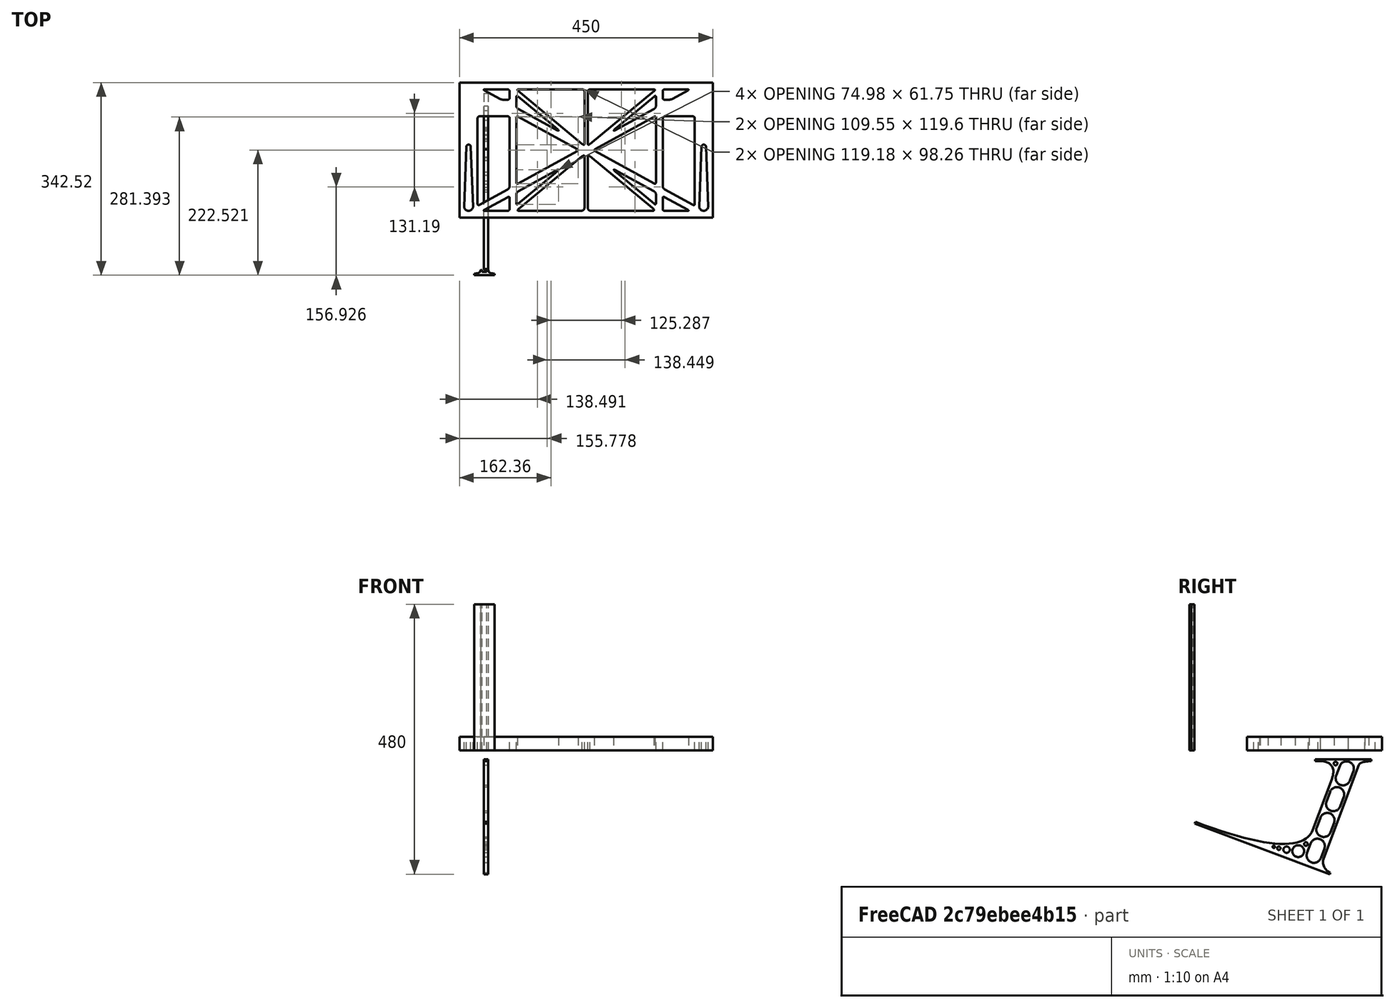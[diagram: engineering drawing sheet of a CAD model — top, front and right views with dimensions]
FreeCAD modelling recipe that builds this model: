
FCSTD DOCUMENT  (FreeCAD 0.19R0.19.2)
Label: laptopStand154FCStd
License: All rights reserved
LicenseURL: http://en.wikipedia.org/wiki/All_rights_reserved
objects: Sketcher::SketchObject×4, Part::Extrusion×3
note: 7 computed .brp shape members not serialized (recipe doc carries the construction recipe); baked Part::Feature solids carry a one-line shape summary decoded from their .brp

FEATURE [Sketcher::SketchObject] Sketch
  FullyConstrained = false
  sketch-geometry (349):
    g0: LineSegment StartX=-10.9272 StartY=-82.7794 StartZ=0 EndX=46.0728 EndY=-51.4823 EndZ=0
    g1: LineSegment StartX=-10.9272 StartY=76.4095 StartZ=0 EndX=-10.9272 EndY=-82.7794 EndZ=0
    g2: LineSegment StartX=46.0728 StartY=76.4095 StartZ=0 EndX=46.0728 EndY=-51.4823 EndZ=0
    g3: LineSegment StartX=-42.9272 StartY=136.221 StartZ=0 EndX=-42.9272 EndY=-103.779 EndZ=0
    g4: LineSegment StartX=407.073 StartY=136.221 StartZ=0 EndX=407.073 EndY=-103.779 EndZ=0
    g5: ArcOfCircle CenterX=-26.9272 CenterY=-83.7794 CenterZ=0 NormalX=0 NormalY=0 NormalZ=1 AngleXU=0 Radius=8 StartAngle=3.14159 EndAngle=6.28319
    g6: ArcOfCircle CenterX=391.073 CenterY=22.1087 CenterZ=0 NormalX=0 NormalY=0 NormalZ=1 AngleXU=0 Radius=8 StartAngle=-4.4e-15 EndAngle=3.14159
    g7: LineSegment StartX=399.073 StartY=22.1087 StartZ=0 EndX=399.073 EndY=-83.7794 EndZ=0
    g8: LineSegment StartX=383.073 StartY=22.1087 StartZ=0 EndX=383.073 EndY=-83.7794 EndZ=0
    g9: ArcOfCircle CenterX=391.073 CenterY=-83.7794 CenterZ=0 NormalX=0 NormalY=0 NormalZ=1 AngleXU=0 Radius=8 StartAngle=3.14159 EndAngle=6.28319
    g10: Circle CenterX=175.022 CenterY=27.0628 CenterZ=0 NormalX=0 NormalY=0 NormalZ=1 AngleXU=0 Radius=1
    g11: Circle CenterX=179.022 CenterY=24.8665 CenterZ=0 NormalX=0 NormalY=0 NormalZ=1 AngleXU=0 Radius=1
    g12: Circle CenterX=179.022 CenterY=27.0628 CenterZ=0 NormalX=0 NormalY=0 NormalZ=1 AngleXU=0 Radius=1
    g13: BSplineCurve PolesCount=3 KnotsCount=2 Degree=2 IsPeriodic=0
    g14: GeomPoint X=175.022 Y=27.0628 Z=0
    g15: GeomPoint X=179.022 Y=27.0628 Z=0
    g16: Circle CenterX=189.124 CenterY=27.0628 CenterZ=0 NormalX=0 NormalY=0 NormalZ=1 AngleXU=0 Radius=1
    g17: Circle CenterX=185.124 CenterY=24.8665 CenterZ=0 NormalX=0 NormalY=0 NormalZ=1 AngleXU=0 Radius=1
    g18: Circle CenterX=185.124 CenterY=27.0628 CenterZ=0 NormalX=0 NormalY=0 NormalZ=1 AngleXU=0 Radius=1
    g19: BSplineCurve PolesCount=3 KnotsCount=2 Degree=2 IsPeriodic=0
    g20: GeomPoint X=189.124 Y=27.0628 Z=0
    g21: GeomPoint X=185.124 Y=27.0628 Z=0
    g22: Circle CenterX=175.022 CenterY=5.37834 CenterZ=0 NormalX=0 NormalY=0 NormalZ=1 AngleXU=0 Radius=1
    g23: Circle CenterX=179.022 CenterY=7.57463 CenterZ=0 NormalX=0 NormalY=0 NormalZ=1 AngleXU=0 Radius=1
    g24: Circle CenterX=179.022 CenterY=5.34704 CenterZ=0 NormalX=0 NormalY=0 NormalZ=1 AngleXU=0 Radius=1
    g25: BSplineCurve PolesCount=3 KnotsCount=2 Degree=2 IsPeriodic=0
    g26: GeomPoint X=175.022 Y=5.37834 Z=0
    g27: GeomPoint X=179.022 Y=5.34704 Z=0
    g28: Circle CenterX=189.124 CenterY=5.37834 CenterZ=0 NormalX=0 NormalY=0 NormalZ=1 AngleXU=0 Radius=1
    g29: Circle CenterX=185.124 CenterY=7.57463 CenterZ=0 NormalX=0 NormalY=0 NormalZ=1 AngleXU=0 Radius=1
    g30: Circle CenterX=185.124 CenterY=5.34704 CenterZ=0 NormalX=0 NormalY=0 NormalZ=1 AngleXU=0 Radius=1
    g31: BSplineCurve PolesCount=3 KnotsCount=2 Degree=2 IsPeriodic=0
    g32: GeomPoint X=189.124 Y=5.37834 Z=0
    g33: GeomPoint X=185.124 Y=5.34704 Z=0
    g34: Circle CenterX=165.871 CenterY=18.1458 CenterZ=0 NormalX=0 NormalY=0 NormalZ=1 AngleXU=0 Radius=1
    g35: Circle CenterX=169.377 CenterY=16.2206 CenterZ=0 NormalX=0 NormalY=0 NormalZ=1 AngleXU=0 Radius=1
    g36: Circle CenterX=165.871 CenterY=14.2954 CenterZ=0 NormalX=0 NormalY=0 NormalZ=1 AngleXU=0 Radius=1
    g37: BSplineCurve PolesCount=3 KnotsCount=2 Degree=2 IsPeriodic=0
    g38: GeomPoint X=165.871 Y=18.1458 Z=0
    g39: GeomPoint X=165.871 Y=14.2954 Z=0
    g40: Circle CenterX=198.275 CenterY=18.1458 CenterZ=0 NormalX=0 NormalY=0 NormalZ=1 AngleXU=0 Radius=1
    g41: Circle CenterX=194.768 CenterY=16.2206 CenterZ=0 NormalX=0 NormalY=0 NormalZ=1 AngleXU=0 Radius=1
    g42: Circle CenterX=198.275 CenterY=14.2954 CenterZ=0 NormalX=0 NormalY=0 NormalZ=1 AngleXU=0 Radius=1
    g43: BSplineCurve PolesCount=3 KnotsCount=2 Degree=2 IsPeriodic=0
    g44: GeomPoint X=198.275 Y=18.1458 Z=0
    g45: GeomPoint X=198.275 Y=14.2954 Z=0
    g46: LineSegment StartX=407.073 StartY=-103.779 StartZ=0 EndX=-42.9272 EndY=-103.779 EndZ=0
    g47: LineSegment StartX=407.073 StartY=136.221 StartZ=0 EndX=-42.9272 EndY=136.221 EndZ=0
    g48: LineSegment StartX=46.0728 StartY=76.4095 StartZ=0 EndX=-10.9272 EndY=76.4095 EndZ=0
    g49: Circle CenterX=125.607 CenterY=54.1951 CenterZ=0 NormalX=0 NormalY=0 NormalZ=1 AngleXU=0 Radius=1
    g50: Circle CenterX=139.632 CenterY=46.4944 CenterZ=0 NormalX=0 NormalY=0 NormalZ=1 AngleXU=0 Radius=1
    g51: Circle CenterX=127.326 CenterY=56.7187 CenterZ=0 NormalX=0 NormalY=0 NormalZ=1 AngleXU=0 Radius=1
    g52: BSplineCurve PolesCount=3 KnotsCount=2 Degree=2 IsPeriodic=0
    g53: GeomPoint X=125.607 Y=54.1951 Z=0
    g54: GeomPoint X=127.326 Y=56.7187 Z=0
    g55: Circle CenterX=236.821 CenterY=56.7187 CenterZ=0 NormalX=0 NormalY=0 NormalZ=1 AngleXU=0 Radius=1
    g56: Circle CenterX=224.513 CenterY=46.4944 CenterZ=0 NormalX=0 NormalY=0 NormalZ=1 AngleXU=0 Radius=1
    g57: Circle CenterX=238.538 CenterY=54.1951 CenterZ=0 NormalX=0 NormalY=0 NormalZ=1 AngleXU=0 Radius=1
    g58: BSplineCurve PolesCount=3 KnotsCount=2 Degree=2 IsPeriodic=0
    g59: GeomPoint X=236.821 Y=56.7187 Z=0
    g60: GeomPoint X=238.538 Y=54.1951 Z=0
    g61: Circle CenterX=238.538 CenterY=-21.7539 CenterZ=0 NormalX=0 NormalY=0 NormalZ=1 AngleXU=0 Radius=1
    g62: Circle CenterX=224.513 CenterY=-14.0532 CenterZ=0 NormalX=0 NormalY=0 NormalZ=1 AngleXU=0 Radius=1
    g63: Circle CenterX=236.821 CenterY=-24.2775 CenterZ=0 NormalX=0 NormalY=0 NormalZ=1 AngleXU=0 Radius=1
    g64: BSplineCurve PolesCount=3 KnotsCount=2 Degree=2 IsPeriodic=0
    g65: GeomPoint X=238.538 Y=-21.7539 Z=0
    g66: GeomPoint X=236.821 Y=-24.2775 Z=0
    g67: Circle CenterX=125.607 CenterY=-21.7539 CenterZ=0 NormalX=0 NormalY=0 NormalZ=1 AngleXU=0 Radius=1
    g68: Circle CenterX=139.632 CenterY=-14.0532 CenterZ=0 NormalX=0 NormalY=0 NormalZ=1 AngleXU=0 Radius=1
    g69: Circle CenterX=127.325 CenterY=-24.2775 CenterZ=0 NormalX=0 NormalY=0 NormalZ=1 AngleXU=0 Radius=1
    g70: BSplineCurve PolesCount=3 KnotsCount=2 Degree=2 IsPeriodic=0
    g71: GeomPoint X=125.607 Y=-21.7539 Z=0
    g72: GeomPoint X=127.325 Y=-24.2775 Z=0
    g73: Circle CenterX=302.996 CenterY=111.695 CenterZ=0 NormalX=0 NormalY=0 NormalZ=1 AngleXU=0 Radius=1
    g74: Circle CenterX=306.073 CenterY=114.251 CenterZ=0 NormalX=0 NormalY=0 NormalZ=1 AngleXU=0 Radius=1
    g75: Circle CenterX=306.073 CenterY=110.251 CenterZ=0 NormalX=0 NormalY=0 NormalZ=1 AngleXU=0 Radius=1
    g76: BSplineCurve PolesCount=3 KnotsCount=2 Degree=2 IsPeriodic=0
    g77: GeomPoint X=302.996 Y=111.695 Z=0
    g78: GeomPoint X=306.073 Y=110.251 Z=0
    g79: Circle CenterX=306.073 CenterY=95.2763 CenterZ=0 NormalX=0 NormalY=0 NormalZ=1 AngleXU=0 Radius=1
    g80: Circle CenterX=306.073 CenterY=91.2763 CenterZ=0 NormalX=0 NormalY=0 NormalZ=1 AngleXU=0 Radius=1
    g81: Circle CenterX=302.567 CenterY=89.3511 CenterZ=0 NormalX=0 NormalY=0 NormalZ=1 AngleXU=0 Radius=1
    g82: BSplineCurve PolesCount=3 KnotsCount=2 Degree=2 IsPeriodic=0
    g83: GeomPoint X=306.073 Y=95.2763 Z=0
    g84: GeomPoint X=302.567 Y=89.3511 Z=0
    g85: LineSegment StartX=306.073 StartY=110.251 StartZ=0 EndX=306.073 EndY=95.2763 EndZ=0
    g86: LineSegment StartX=302.996 StartY=111.695 StartZ=0 EndX=236.821 EndY=56.7187 EndZ=0
    g87: LineSegment StartX=238.538 StartY=54.1951 StartZ=0 EndX=302.567 EndY=89.3511 EndZ=0
    g88: Circle CenterX=61.1496 CenterY=111.695 CenterZ=0 NormalX=0 NormalY=0 NormalZ=1 AngleXU=0 Radius=1
    g89: Circle CenterX=58.0728 CenterY=114.251 CenterZ=0 NormalX=0 NormalY=0 NormalZ=1 AngleXU=0 Radius=1
    g90: Circle CenterX=58.0728 CenterY=110.251 CenterZ=0 NormalX=0 NormalY=0 NormalZ=1 AngleXU=0 Radius=1
    g91: BSplineCurve PolesCount=3 KnotsCount=2 Degree=2 IsPeriodic=0
    g92: GeomPoint X=61.1496 Y=111.695 Z=0
    g93: GeomPoint X=58.0728 Y=110.251 Z=0
    g94: Circle CenterX=61.5791 CenterY=89.3511 CenterZ=0 NormalX=0 NormalY=0 NormalZ=1 AngleXU=0 Radius=1
    g95: Circle CenterX=58.0728 CenterY=91.2763 CenterZ=0 NormalX=0 NormalY=0 NormalZ=1 AngleXU=0 Radius=1
    g96: Circle CenterX=58.0728 CenterY=95.2763 CenterZ=0 NormalX=0 NormalY=0 NormalZ=1 AngleXU=0 Radius=1
    g97: BSplineCurve PolesCount=3 KnotsCount=2 Degree=2 IsPeriodic=0
    g98: GeomPoint X=61.5791 Y=89.3511 Z=0
    g99: GeomPoint X=58.0728 Y=95.2763 Z=0
    g100: LineSegment StartX=58.0728 StartY=110.251 StartZ=0 EndX=58.0728 EndY=95.2763 EndZ=0
    g101: LineSegment StartX=61.1496 StartY=111.695 StartZ=0 EndX=127.326 EndY=56.7187 EndZ=0
    g102: LineSegment StartX=125.607 StartY=54.1951 StartZ=0 EndX=61.5791 EndY=89.3511 EndZ=0
    g103: Circle CenterX=61.5791 CenterY=-56.9099 CenterZ=0 NormalX=0 NormalY=0 NormalZ=1 AngleXU=0 Radius=1
    g104: Circle CenterX=58.0728 CenterY=-58.8351 CenterZ=0 NormalX=0 NormalY=0 NormalZ=1 AngleXU=0 Radius=1
    g105: Circle CenterX=58.0728 CenterY=-62.8351 CenterZ=0 NormalX=0 NormalY=0 NormalZ=1 AngleXU=0 Radius=1
    g106: BSplineCurve PolesCount=3 KnotsCount=2 Degree=2 IsPeriodic=0
    g107: GeomPoint X=61.5791 Y=-56.9099 Z=0
    g108: GeomPoint X=58.0728 Y=-62.8351 Z=0
    g109: Circle CenterX=58.0728 CenterY=-77.8102 CenterZ=0 NormalX=0 NormalY=0 NormalZ=1 AngleXU=0 Radius=1
    g110: Circle CenterX=58.0728 CenterY=-81.8102 CenterZ=0 NormalX=0 NormalY=0 NormalZ=1 AngleXU=0 Radius=1
    g111: Circle CenterX=61.1496 CenterY=-79.2541 CenterZ=0 NormalX=0 NormalY=0 NormalZ=1 AngleXU=0 Radius=1
    g112: BSplineCurve PolesCount=3 KnotsCount=2 Degree=2 IsPeriodic=0
    g113: GeomPoint X=58.0728 Y=-77.8102 Z=0
    g114: GeomPoint X=61.1496 Y=-79.2541 Z=0
    g115: LineSegment StartX=58.0728 StartY=-62.8351 StartZ=0 EndX=58.0728 EndY=-77.8102 EndZ=0
    g116: LineSegment StartX=61.1496 StartY=-79.2541 StartZ=0 EndX=127.325 EndY=-24.2775 EndZ=0
    g117: LineSegment StartX=125.607 StartY=-21.7539 StartZ=0 EndX=61.5791 EndY=-56.9099 EndZ=0
    g118: Circle CenterX=302.567 CenterY=-56.9099 CenterZ=0 NormalX=0 NormalY=0 NormalZ=1 AngleXU=0 Radius=1
    g119: Circle CenterX=306.073 CenterY=-58.8351 CenterZ=0 NormalX=0 NormalY=0 NormalZ=1 AngleXU=0 Radius=1
    g120: Circle CenterX=306.073 CenterY=-62.8351 CenterZ=0 NormalX=0 NormalY=0 NormalZ=1 AngleXU=0 Radius=1
    g121: BSplineCurve PolesCount=3 KnotsCount=2 Degree=2 IsPeriodic=0
    g122: GeomPoint X=302.567 Y=-56.9099 Z=0
    g123: GeomPoint X=306.073 Y=-62.8351 Z=0
    g124: Circle CenterX=302.996 CenterY=-79.2541 CenterZ=0 NormalX=0 NormalY=0 NormalZ=1 AngleXU=0 Radius=1
    g125: Circle CenterX=306.073 CenterY=-81.8102 CenterZ=0 NormalX=0 NormalY=0 NormalZ=1 AngleXU=0 Radius=1
    g126: Circle CenterX=306.073 CenterY=-77.8102 CenterZ=0 NormalX=0 NormalY=0 NormalZ=1 AngleXU=0 Radius=1
    g127: BSplineCurve PolesCount=3 KnotsCount=2 Degree=2 IsPeriodic=0
    g128: GeomPoint X=302.996 Y=-79.2541 Z=0
    g129: GeomPoint X=306.073 Y=-77.8102 Z=0
    g130: LineSegment StartX=306.073 StartY=-62.8351 StartZ=0 EndX=306.073 EndY=-77.8102 EndZ=0
    g131: LineSegment StartX=302.996 StartY=-79.2541 StartZ=0 EndX=236.821 EndY=-24.2775 EndZ=0
    g132: LineSegment StartX=238.538 StartY=-21.7539 StartZ=0 EndX=302.567 EndY=-56.9099 EndZ=0
    g133: Circle CenterX=61.6457 CenterY=-88.8112 CenterZ=0 NormalX=0 NormalY=0 NormalZ=1 AngleXU=0 Radius=1
    g134: Circle CenterX=58.0728 CenterY=-91.7794 CenterZ=0 NormalX=0 NormalY=0 NormalZ=1 AngleXU=0 Radius=1
    g135: Circle CenterX=63.9135 CenterY=-91.7794 CenterZ=0 NormalX=0 NormalY=0 NormalZ=1 AngleXU=0 Radius=1
    g136: BSplineCurve PolesCount=3 KnotsCount=2 Degree=2 IsPeriodic=0
    g137: GeomPoint X=61.6457 Y=-88.8112 Z=0
    g138: GeomPoint X=63.9135 Y=-91.7794 Z=0
    g139: Circle CenterX=179.022 CenterY=-85.8163 CenterZ=0 NormalX=0 NormalY=0 NormalZ=1 AngleXU=0 Radius=1
    g140: Circle CenterX=179.022 CenterY=-91.7794 CenterZ=0 NormalX=0 NormalY=0 NormalZ=1 AngleXU=0 Radius=1
    g141: Circle CenterX=171.895 CenterY=-91.7794 CenterZ=0 NormalX=0 NormalY=0 NormalZ=1 AngleXU=0 Radius=1
    g142: BSplineCurve PolesCount=3 KnotsCount=2 Degree=2 IsPeriodic=0
    g143: GeomPoint X=179.022 Y=-85.8163 Z=0
    g144: GeomPoint X=171.895 Y=-91.7794 Z=0
    g145: Circle CenterX=185.124 CenterY=-86.2028 CenterZ=0 NormalX=0 NormalY=0 NormalZ=1 AngleXU=0 Radius=1
    g146: Circle CenterX=185.124 CenterY=-91.7794 CenterZ=0 NormalX=0 NormalY=0 NormalZ=1 AngleXU=0 Radius=1
    g147: Circle CenterX=191.747 CenterY=-91.7794 CenterZ=0 NormalX=0 NormalY=0 NormalZ=1 AngleXU=0 Radius=1
    g148: BSplineCurve PolesCount=3 KnotsCount=2 Degree=2 IsPeriodic=0
    g149: GeomPoint X=185.124 Y=-86.2028 Z=0
    g150: GeomPoint X=191.747 Y=-91.7794 Z=0
    g151: Circle CenterX=299.888 CenterY=-86.6413 CenterZ=0 NormalX=0 NormalY=0 NormalZ=1 AngleXU=0 Radius=1
    g152: Circle CenterX=306.073 CenterY=-91.7794 CenterZ=0 NormalX=0 NormalY=0 NormalZ=1 AngleXU=0 Radius=1
    g153: Circle CenterX=298.776 CenterY=-91.7794 CenterZ=0 NormalX=0 NormalY=0 NormalZ=1 AngleXU=0 Radius=1
    g154: BSplineCurve PolesCount=3 KnotsCount=2 Degree=2 IsPeriodic=0
    g155: GeomPoint X=299.888 Y=-86.6413 Z=0
    g156: GeomPoint X=298.776 Y=-91.7794 Z=0
    g157: LineSegment StartX=189.124 StartY=5.37834 StartZ=0 EndX=299.888 EndY=-86.6413 EndZ=0
    g158: LineSegment StartX=298.776 StartY=-91.7794 StartZ=0 EndX=191.747 EndY=-91.7794 EndZ=0
    g159: LineSegment StartX=185.124 StartY=-86.2028 StartZ=0 EndX=185.124 EndY=5.34704 EndZ=0
    g160: LineSegment StartX=179.022 StartY=5.34704 StartZ=0 EndX=179.022 EndY=-85.8163 EndZ=0
    g161: LineSegment StartX=171.895 StartY=-91.7794 StartZ=0 EndX=63.9135 EndY=-91.7794 EndZ=0
    g162: LineSegment StartX=61.6457 StartY=-88.8112 StartZ=0 EndX=175.022 EndY=5.37834 EndZ=0
    g163: Circle CenterX=302.073 CenterY=124.221 CenterZ=0 NormalX=0 NormalY=0 NormalZ=1 AngleXU=0 Radius=1
    g164: Circle CenterX=306.073 CenterY=124.221 CenterZ=0 NormalX=0 NormalY=0 NormalZ=1 AngleXU=0 Radius=1
    g165: Circle CenterX=302.996 CenterY=121.665 CenterZ=0 NormalX=0 NormalY=0 NormalZ=1 AngleXU=0 Radius=1
    g166: BSplineCurve PolesCount=3 KnotsCount=2 Degree=2 IsPeriodic=0
    g167: GeomPoint X=302.073 Y=124.221 Z=0
    g168: GeomPoint X=302.996 Y=121.665 Z=0
    g169: Circle CenterX=189.124 CenterY=124.221 CenterZ=0 NormalX=0 NormalY=0 NormalZ=1 AngleXU=0 Radius=1
    g170: Circle CenterX=185.124 CenterY=124.221 CenterZ=0 NormalX=0 NormalY=0 NormalZ=1 AngleXU=0 Radius=1
    g171: Circle CenterX=185.124 CenterY=120.221 CenterZ=0 NormalX=0 NormalY=0 NormalZ=1 AngleXU=0 Radius=1
    g172: BSplineCurve PolesCount=3 KnotsCount=2 Degree=2 IsPeriodic=0
    g173: GeomPoint X=189.124 Y=124.221 Z=0
    g174: GeomPoint X=185.124 Y=120.221 Z=0
    g175: Circle CenterX=175.022 CenterY=124.221 CenterZ=0 NormalX=0 NormalY=0 NormalZ=1 AngleXU=0 Radius=1
    g176: Circle CenterX=179.022 CenterY=124.221 CenterZ=0 NormalX=0 NormalY=0 NormalZ=1 AngleXU=0 Radius=1
    g177: Circle CenterX=179.022 CenterY=120.221 CenterZ=0 NormalX=0 NormalY=0 NormalZ=1 AngleXU=0 Radius=1
    g178: BSplineCurve PolesCount=3 KnotsCount=2 Degree=2 IsPeriodic=0
    g179: GeomPoint X=175.022 Y=124.221 Z=0
    g180: GeomPoint X=179.022 Y=120.221 Z=0
    g181: Circle CenterX=62.0728 CenterY=124.221 CenterZ=0 NormalX=0 NormalY=0 NormalZ=1 AngleXU=0 Radius=1
    g182: Circle CenterX=58.0728 CenterY=124.221 CenterZ=0 NormalX=0 NormalY=0 NormalZ=1 AngleXU=0 Radius=1
    g183: Circle CenterX=61.1496 CenterY=121.665 CenterZ=0 NormalX=0 NormalY=0 NormalZ=1 AngleXU=0 Radius=1
    g184: BSplineCurve PolesCount=3 KnotsCount=2 Degree=2 IsPeriodic=0
    g185: GeomPoint X=62.0728 Y=124.221 Z=0
    g186: GeomPoint X=61.1496 Y=121.665 Z=0
    g187: LineSegment StartX=62.0728 StartY=124.221 StartZ=0 EndX=175.022 EndY=124.221 EndZ=0
    g188: LineSegment StartX=179.022 StartY=120.221 StartZ=0 EndX=179.022 EndY=27.0628 EndZ=0
    g189: LineSegment StartX=185.124 StartY=27.0628 StartZ=0 EndX=185.124 EndY=120.221 EndZ=0
    g190: LineSegment StartX=189.124 StartY=124.221 StartZ=0 EndX=302.073 EndY=124.221 EndZ=0
    g191: LineSegment StartX=302.996 StartY=121.665 StartZ=0 EndX=189.124 EndY=27.0628 EndZ=0
    g192: LineSegment StartX=175.022 StartY=27.0628 StartZ=0 EndX=61.1496 EndY=121.665 EndZ=0
    g193: Circle CenterX=61.5791 CenterY=75.4095 CenterZ=0 NormalX=0 NormalY=0 NormalZ=1 AngleXU=0 Radius=1
    g194: Circle CenterX=58.0728 CenterY=77.3346 CenterZ=0 NormalX=0 NormalY=0 NormalZ=1 AngleXU=0 Radius=1
    g195: Circle CenterX=58.0728 CenterY=73.3346 CenterZ=0 NormalX=0 NormalY=0 NormalZ=1 AngleXU=0 Radius=1
    g196: BSplineCurve PolesCount=3 KnotsCount=2 Degree=2 IsPeriodic=0
    g197: GeomPoint X=61.5791 Y=75.4095 Z=0
    g198: GeomPoint X=58.0728 Y=73.3346 Z=0
    g199: Circle CenterX=58.0728 CenterY=-40.8935 CenterZ=0 NormalX=0 NormalY=0 NormalZ=1 AngleXU=0 Radius=1
    g200: Circle CenterX=58.0728 CenterY=-44.8935 CenterZ=0 NormalX=0 NormalY=0 NormalZ=1 AngleXU=0 Radius=1
    g201: Circle CenterX=61.5791 CenterY=-42.9683 CenterZ=0 NormalX=0 NormalY=0 NormalZ=1 AngleXU=0 Radius=1
    g202: BSplineCurve PolesCount=3 KnotsCount=2 Degree=2 IsPeriodic=0
    g203: GeomPoint X=58.0728 Y=-40.8935 Z=0
    g204: GeomPoint X=61.5791 Y=-42.9683 Z=0
    g205: LineSegment StartX=61.5791 StartY=-42.9683 StartZ=0 EndX=165.871 EndY=14.2954 EndZ=0
    g206: LineSegment StartX=165.871 StartY=18.1458 StartZ=0 EndX=61.5791 EndY=75.4095 EndZ=0
    g207: LineSegment StartX=58.0728 StartY=73.3346 StartZ=0 EndX=58.0728 EndY=-40.8935 EndZ=0
    g208: Circle CenterX=302.567 CenterY=-42.9683 CenterZ=0 NormalX=0 NormalY=0 NormalZ=1 AngleXU=0 Radius=1
    g209: Circle CenterX=306.073 CenterY=-44.8935 CenterZ=0 NormalX=0 NormalY=0 NormalZ=1 AngleXU=0 Radius=1
    g210: Circle CenterX=306.073 CenterY=-40.8935 CenterZ=0 NormalX=0 NormalY=0 NormalZ=1 AngleXU=0 Radius=1
    g211: BSplineCurve PolesCount=3 KnotsCount=2 Degree=2 IsPeriodic=0
    g212: GeomPoint X=302.567 Y=-42.9683 Z=0
    g213: GeomPoint X=306.073 Y=-40.8935 Z=0
    g214: Circle CenterX=306.073 CenterY=73.3346 CenterZ=0 NormalX=0 NormalY=0 NormalZ=1 AngleXU=0 Radius=1
    g215: Circle CenterX=306.073 CenterY=77.3346 CenterZ=0 NormalX=0 NormalY=0 NormalZ=1 AngleXU=0 Radius=1
    g216: Circle CenterX=302.567 CenterY=75.4095 CenterZ=0 NormalX=0 NormalY=0 NormalZ=1 AngleXU=0 Radius=1
    g217: BSplineCurve PolesCount=3 KnotsCount=2 Degree=2 IsPeriodic=0
    g218: GeomPoint X=306.073 Y=73.3346 Z=0
    g219: GeomPoint X=302.567 Y=75.4095 Z=0
    g220: LineSegment StartX=302.567 StartY=-42.9683 StartZ=0 EndX=198.275 EndY=14.2954 EndZ=0
    g221: LineSegment StartX=198.275 StartY=18.1458 StartZ=0 EndX=302.567 EndY=75.4095 EndZ=0
    g222: LineSegment StartX=306.073 StartY=73.3346 StartZ=0 EndX=306.073 EndY=-40.8935 EndZ=0
    g223: LineSegment StartX=322.073 StartY=105.865 StartZ=0 EndX=328.643 EndY=105.865 EndZ=0
    g224: LineSegment StartX=318.073 StartY=120.221 StartZ=0 EndX=318.073 EndY=109.865 EndZ=0
    g225: LineSegment StartX=336.157 StartY=107.779 StartZ=0 EndX=362.567 EndY=122.294 EndZ=0
    g226: Circle CenterX=362.073 CenterY=124.221 CenterZ=0 NormalX=0 NormalY=0 NormalZ=1 AngleXU=0 Radius=1
    g227: Circle CenterX=366.073 CenterY=124.221 CenterZ=0 NormalX=0 NormalY=0 NormalZ=1 AngleXU=0 Radius=1
    g228: Circle CenterX=362.567 CenterY=122.294 CenterZ=0 NormalX=0 NormalY=0 NormalZ=1 AngleXU=0 Radius=1
    g229: BSplineCurve PolesCount=3 KnotsCount=2 Degree=2 IsPeriodic=0
    g230: GeomPoint X=362.073 Y=124.221 Z=0
    g231: GeomPoint X=362.567 Y=122.294 Z=0
    g232: Circle CenterX=322.073 CenterY=124.221 CenterZ=0 NormalX=0 NormalY=0 NormalZ=1 AngleXU=0 Radius=1
    g233: Circle CenterX=318.073 CenterY=124.221 CenterZ=0 NormalX=0 NormalY=0 NormalZ=1 AngleXU=0 Radius=1
    g234: Circle CenterX=318.073 CenterY=120.221 CenterZ=0 NormalX=0 NormalY=0 NormalZ=1 AngleXU=0 Radius=1
    g235: BSplineCurve PolesCount=3 KnotsCount=2 Degree=2 IsPeriodic=0
    g236: GeomPoint X=322.073 Y=124.221 Z=0
    g237: GeomPoint X=318.073 Y=120.221 Z=0
    g238: Circle CenterX=322.073 CenterY=105.865 CenterZ=0 NormalX=0 NormalY=0 NormalZ=1 AngleXU=0 Radius=1
    g239: Circle CenterX=318.073 CenterY=105.865 CenterZ=0 NormalX=0 NormalY=0 NormalZ=1 AngleXU=0 Radius=1
    g240: Circle CenterX=318.073 CenterY=109.865 CenterZ=0 NormalX=0 NormalY=0 NormalZ=1 AngleXU=0 Radius=1
    g241: BSplineCurve PolesCount=3 KnotsCount=2 Degree=2 IsPeriodic=0
    g242: GeomPoint X=322.073 Y=105.865 Z=0
    g243: GeomPoint X=318.073 Y=109.865 Z=0
    g244: Circle CenterX=336.157 CenterY=107.779 CenterZ=0 NormalX=0 NormalY=0 NormalZ=1 AngleXU=0 Radius=1
    g245: Circle CenterX=332.651 CenterY=105.853 CenterZ=0 NormalX=0 NormalY=0 NormalZ=1 AngleXU=0 Radius=1
    g246: Circle CenterX=328.643 CenterY=105.865 CenterZ=0 NormalX=0 NormalY=0 NormalZ=1 AngleXU=0 Radius=1
    g247: BSplineCurve PolesCount=3 KnotsCount=2 Degree=2 IsPeriodic=0
    g248: GeomPoint X=336.157 Y=107.779 Z=0
    g249: GeomPoint X=328.643 Y=105.865 Z=0
    g250: LineSegment StartX=322.073 StartY=124.221 StartZ=0 EndX=362.073 EndY=124.221 EndZ=0
    g251: Circle CenterX=371.567 CenterY=-80.8644 CenterZ=0 NormalX=0 NormalY=0 NormalZ=1 AngleXU=0 Radius=1
    g252: Circle CenterX=375.073 CenterY=-82.7896 CenterZ=0 NormalX=0 NormalY=0 NormalZ=1 AngleXU=0 Radius=1
    g253: Circle CenterX=375.073 CenterY=-78.7896 CenterZ=0 NormalX=0 NormalY=0 NormalZ=1 AngleXU=0 Radius=1
    g254: BSplineCurve PolesCount=3 KnotsCount=2 Degree=2 IsPeriodic=0
    g255: GeomPoint X=371.567 Y=-80.8644 Z=0
    g256: GeomPoint X=375.073 Y=-78.7896 Z=0
    g257: Circle CenterX=321.579 CenterY=-53.4075 CenterZ=0 NormalX=0 NormalY=0 NormalZ=1 AngleXU=0 Radius=1
    g258: Circle CenterX=318.073 CenterY=-51.4823 CenterZ=0 NormalX=0 NormalY=0 NormalZ=1 AngleXU=0 Radius=1
    g259: Circle CenterX=318.073 CenterY=-47.4805 CenterZ=0 NormalX=0 NormalY=0 NormalZ=1 AngleXU=0 Radius=1
    g260: BSplineCurve PolesCount=3 KnotsCount=2 Degree=2 IsPeriodic=0
    g261: GeomPoint X=321.579 Y=-53.4075 Z=0
    g262: GeomPoint X=318.073 Y=-47.4805 Z=0
    g263: LineSegment StartX=371.567 StartY=-80.8644 StartZ=0 EndX=321.579 EndY=-53.4075 EndZ=0
    g264: Circle CenterX=321.579 CenterY=-67.3492 CenterZ=0 NormalX=0 NormalY=0 NormalZ=1 AngleXU=0 Radius=1
    g265: Circle CenterX=318.073 CenterY=-65.424 CenterZ=0 NormalX=0 NormalY=0 NormalZ=1 AngleXU=0 Radius=1
    g266: Circle CenterX=318.073 CenterY=-69.424 CenterZ=0 NormalX=0 NormalY=0 NormalZ=1 AngleXU=0 Radius=1
    g267: BSplineCurve PolesCount=3 KnotsCount=2 Degree=2 IsPeriodic=0
    g268: GeomPoint X=321.579 Y=-67.3492 Z=0
    g269: GeomPoint X=318.073 Y=-69.424 Z=0
    g270: Circle CenterX=362.567 CenterY=-89.8542 CenterZ=0 NormalX=0 NormalY=0 NormalZ=1 AngleXU=0 Radius=1
    g271: Circle CenterX=366.073 CenterY=-91.7794 CenterZ=0 NormalX=0 NormalY=0 NormalZ=1 AngleXU=0 Radius=1
    g272: Circle CenterX=362.073 CenterY=-91.7794 CenterZ=0 NormalX=0 NormalY=0 NormalZ=1 AngleXU=0 Radius=1
    g273: BSplineCurve PolesCount=3 KnotsCount=2 Degree=2 IsPeriodic=0
    g274: GeomPoint X=362.567 Y=-89.8542 Z=0
    g275: GeomPoint X=362.073 Y=-91.7794 Z=0
    g276: Circle CenterX=322.073 CenterY=-91.7794 CenterZ=0 NormalX=0 NormalY=0 NormalZ=1 AngleXU=0 Radius=1
    g277: Circle CenterX=318.073 CenterY=-91.7794 CenterZ=0 NormalX=0 NormalY=0 NormalZ=1 AngleXU=0 Radius=1
    g278: Circle CenterX=318.073 CenterY=-87.7794 CenterZ=0 NormalX=0 NormalY=0 NormalZ=1 AngleXU=0 Radius=1
    g279: BSplineCurve PolesCount=3 KnotsCount=2 Degree=2 IsPeriodic=0
    g280: GeomPoint X=322.073 Y=-91.7794 Z=0
    g281: GeomPoint X=318.073 Y=-87.7794 Z=0
    g282: LineSegment StartX=362.567 StartY=-89.8542 StartZ=0 EndX=321.579 EndY=-67.3492 EndZ=0
    g283: LineSegment StartX=318.073 StartY=-69.424 StartZ=0 EndX=318.073 EndY=-87.7794 EndZ=0
    g284: LineSegment StartX=322.073 StartY=-91.7794 StartZ=0 EndX=362.073 EndY=-91.7794 EndZ=0
    g285: Circle CenterX=2.07281 CenterY=124.221 CenterZ=0 NormalX=0 NormalY=0 NormalZ=1 AngleXU=0 Radius=1
    g286: Circle CenterX=1.57905 CenterY=122.295 CenterZ=0 NormalX=0 NormalY=0 NormalZ=1 AngleXU=0 Radius=1
    g287: BSplineCurve PolesCount=3 KnotsCount=2 Degree=2 IsPeriodic=0
    g288: GeomPoint X=2.07281 Y=124.221 Z=0
    g289: GeomPoint X=1.57905 Y=122.295 Z=0
    g290: Circle CenterX=42.0728 CenterY=124.221 CenterZ=0 NormalX=0 NormalY=0 NormalZ=1 AngleXU=0 Radius=1
    g291: Circle CenterX=46.0728 CenterY=124.221 CenterZ=0 NormalX=0 NormalY=0 NormalZ=1 AngleXU=0 Radius=1
    g292: Circle CenterX=46.0728 CenterY=120.221 CenterZ=0 NormalX=0 NormalY=0 NormalZ=1 AngleXU=0 Radius=1
    g293: BSplineCurve PolesCount=3 KnotsCount=2 Degree=2 IsPeriodic=0
    g294: GeomPoint X=42.0728 Y=124.221 Z=0
    g295: GeomPoint X=46.0728 Y=120.221 Z=0
    g296: Circle CenterX=46.0728 CenterY=109.865 CenterZ=0 NormalX=0 NormalY=0 NormalZ=1 AngleXU=0 Radius=1
    g297: Circle CenterX=46.0728 CenterY=105.865 CenterZ=0 NormalX=0 NormalY=0 NormalZ=1 AngleXU=0 Radius=1
    g298: Circle CenterX=42.0728 CenterY=105.865 CenterZ=0 NormalX=0 NormalY=0 NormalZ=1 AngleXU=0 Radius=1
    g299: BSplineCurve PolesCount=3 KnotsCount=2 Degree=2 IsPeriodic=0
    g300: GeomPoint X=46.0728 Y=109.865 Z=0
    g301: GeomPoint X=42.0728 Y=105.865 Z=0
    g302: Circle CenterX=35.5028 CenterY=105.865 CenterZ=0 NormalX=0 NormalY=0 NormalZ=1 AngleXU=0 Radius=1
    g303: Circle CenterX=31.5028 CenterY=105.865 CenterZ=0 NormalX=0 NormalY=0 NormalZ=1 AngleXU=0 Radius=1
    g304: Circle CenterX=27.9965 CenterY=107.79 CenterZ=0 NormalX=0 NormalY=0 NormalZ=1 AngleXU=0 Radius=1
    g305: BSplineCurve PolesCount=3 KnotsCount=2 Degree=2 IsPeriodic=0
    g306: GeomPoint X=35.5028 Y=105.865 Z=0
    g307: GeomPoint X=27.9965 Y=107.79 Z=0
    g308: LineSegment StartX=2.07281 StartY=124.221 StartZ=0 EndX=42.0728 EndY=124.221 EndZ=0
    g309: LineSegment StartX=46.0728 StartY=120.221 StartZ=0 EndX=46.0728 EndY=109.865 EndZ=0
    g310: LineSegment StartX=42.0728 StartY=105.865 StartZ=0 EndX=35.5028 EndY=105.865 EndZ=0
    g311: LineSegment StartX=27.9965 StartY=107.79 StartZ=0 EndX=1.57905 EndY=122.295 EndZ=0
    g312: Circle CenterX=42.5666 CenterY=-67.3492 CenterZ=0 NormalX=0 NormalY=0 NormalZ=1 AngleXU=0 Radius=1
    g313: Circle CenterX=46.0728 CenterY=-65.424 CenterZ=0 NormalX=0 NormalY=0 NormalZ=1 AngleXU=0 Radius=1
    g314: Circle CenterX=46.0728 CenterY=-69.424 CenterZ=0 NormalX=0 NormalY=0 NormalZ=1 AngleXU=0 Radius=1
    g315: BSplineCurve PolesCount=3 KnotsCount=2 Degree=2 IsPeriodic=0
    g316: GeomPoint X=42.5666 Y=-67.3492 Z=0
    g317: GeomPoint X=46.0728 Y=-69.424 Z=0
    g318: Circle CenterX=46.0728 CenterY=-87.7794 CenterZ=0 NormalX=0 NormalY=0 NormalZ=1 AngleXU=0 Radius=1
    g319: Circle CenterX=46.0728 CenterY=-91.7794 CenterZ=0 NormalX=0 NormalY=0 NormalZ=1 AngleXU=0 Radius=1
    g320: Circle CenterX=42.0728 CenterY=-91.7794 CenterZ=0 NormalX=0 NormalY=0 NormalZ=1 AngleXU=0 Radius=1
    g321: BSplineCurve PolesCount=3 KnotsCount=2 Degree=2 IsPeriodic=0
    g322: GeomPoint X=46.0728 Y=-87.7794 Z=0
    g323: GeomPoint X=42.0728 Y=-91.7794 Z=0
    g324: Circle CenterX=2.07281 CenterY=-91.7794 CenterZ=0 NormalX=0 NormalY=0 NormalZ=1 AngleXU=0 Radius=1
    g325: Circle CenterX=-1.92719 CenterY=-91.7794 CenterZ=0 NormalX=0 NormalY=0 NormalZ=1 AngleXU=0 Radius=1
    g326: Circle CenterX=1.57905 CenterY=-89.8542 CenterZ=0 NormalX=0 NormalY=0 NormalZ=1 AngleXU=0 Radius=1
    g327: BSplineCurve PolesCount=3 KnotsCount=2 Degree=2 IsPeriodic=0
    g328: GeomPoint X=2.07281 Y=-91.7794 Z=0
    g329: GeomPoint X=1.57905 Y=-89.8542 Z=0
    g330: LineSegment StartX=2.07281 StartY=-91.7794 StartZ=0 EndX=42.0728 EndY=-91.7794 EndZ=0
    g331: LineSegment StartX=46.0728 StartY=-87.7794 StartZ=0 EndX=46.0728 EndY=-69.424 EndZ=0
    g332: LineSegment StartX=42.5666 StartY=-67.3492 StartZ=0 EndX=1.57905 EndY=-89.8542 EndZ=0
    g333: Circle CenterX=322.073 CenterY=76.4095 CenterZ=0 NormalX=0 NormalY=0 NormalZ=1 AngleXU=0 Radius=4
    g334: BSplineCurve PolesCount=3 KnotsCount=2 Degree=2 IsPeriodic=0
    g335: GeomPoint X=318.073 Y=72.4095 Z=0
    g336: GeomPoint X=322.073 Y=76.4095 Z=0
    g337: Circle CenterX=375.073 CenterY=72.4095 CenterZ=0 NormalX=0 NormalY=0 NormalZ=1 AngleXU=0 Radius=1
    g338: Circle CenterX=375.073 CenterY=76.4095 CenterZ=0 NormalX=0 NormalY=0 NormalZ=1 AngleXU=0 Radius=1
    g339: Circle CenterX=371.073 CenterY=76.4095 CenterZ=0 NormalX=0 NormalY=0 NormalZ=1 AngleXU=0 Radius=1
    g340: BSplineCurve PolesCount=3 KnotsCount=2 Degree=2 IsPeriodic=0
    g341: GeomPoint X=375.073 Y=72.4095 Z=0
    g342: GeomPoint X=371.073 Y=76.4095 Z=0
    g343: LineSegment StartX=322.073 StartY=76.4095 StartZ=0 EndX=371.073 EndY=76.4095 EndZ=0
    g344: LineSegment StartX=318.073 StartY=72.4095 StartZ=0 EndX=318.073 EndY=-47.4805 EndZ=0
    g345: LineSegment StartX=375.073 StartY=72.4095 StartZ=0 EndX=375.073 EndY=-78.7896 EndZ=0
    g346: ArcOfCircle CenterX=-26.9272 CenterY=22.1087 CenterZ=0 NormalX=0 NormalY=0 NormalZ=1 AngleXU=0 Radius=4 StartAngle=5e-16 EndAngle=3.14159
    g347: LineSegment StartX=-30.9272 StartY=22.1087 StartZ=0 EndX=-34.9272 EndY=-83.7794 EndZ=0
    g348: LineSegment StartX=-18.9272 StartY=-83.7794 StartZ=0 EndX=-22.9272 EndY=22.1087 EndZ=0
  constraints (572):
    c: Coincident(g0,g2)
    c: Block(g0)
    c: Block(g1)
    c: Vertical(g3)
    c: Vertical(g4)
    c: Block(g4)
    c: Block(g3)
    c: Tangent(g6,g7) = 1.5708
    c: Tangent(g7,g9) = 1.5708
    c: Equal(g6,g9)
    c: Coincident(g8,g6)
    c: Coincident(g8,g9)
    c: Block(g7)
    c: Block(g8)
    c: Weight(g10) = 1
    c: Equal(g10,g11)
    c: Equal(g10,g12)
    c: InternalAlignment(g10,g13)
    c: InternalAlignment(g11,g13)
    c: InternalAlignment(g12,g13)
    c: InternalAlignment(g14,g13)
    c: InternalAlignment(g15,g13)
    c: Weight(g16) = 1
    c: Equal(g16,g17)
    c: Equal(g16,g18)
    c: InternalAlignment(g16,g19)
    c: InternalAlignment(g17,g19)
    c: InternalAlignment(g18,g19)
    c: InternalAlignment(g20,g19)
    c: InternalAlignment(g21,g19)
    c: Block(g19)
    c: Block(g13)
    c: Weight(g22) = 1
    c: Equal(g22,g23)
    c: Equal(g22,g24)
    c: InternalAlignment(g22,g25)
    c: InternalAlignment(g23,g25)
    c: InternalAlignment(g24,g25)
    c: InternalAlignment(g26,g25)
    c: InternalAlignment(g27,g25)
    c: Weight(g28) = 1
    c: Equal(g28,g29)
    c: Equal(g28,g30)
    c: InternalAlignment(g28,g31)
    c: InternalAlignment(g29,g31)
    c: InternalAlignment(g30,g31)
    c: InternalAlignment(g32,g31)
    c: InternalAlignment(g33,g31)
    c: Block(g31)
    c: Block(g25)
    c: Weight(g34) = 1
    c: Equal(g34,g35)
    c: Equal(g34,g36)
    c: InternalAlignment(g34,g37)
    c: InternalAlignment(g35,g37)
    c: InternalAlignment(g36,g37)
    c: InternalAlignment(g38,g37)
    c: InternalAlignment(g39,g37)
    c: Weight(g40) = 1
    c: Equal(g40,g41)
    c: Equal(g40,g42)
    c: InternalAlignment(g40,g43)
    c: InternalAlignment(g41,g43)
    c: InternalAlignment(g42,g43)
    c: InternalAlignment(g44,g43)
    c: InternalAlignment(g45,g43)
    c: Block(g37)
    c: Block(g43)
    c: Coincident(g46,g4)
    c: Coincident(g46,g3)
    c: Horizontal(g46)
    c: Distance(g46) = 450
    c: Coincident(g47,g4)
    c: Coincident(g47,g3)
    c: Horizontal(g47)
    c: Horizontal(g48)
    c: Coincident(g2,g48)
    c: Block(g48)
    c: Coincident(g1,g48)
    c: Weight(g49) = 1
    c: Equal(g49,g50)
    c: Equal(g49,g51)
    c: InternalAlignment(g49,g52)
    c: InternalAlignment(g50,g52)
    c: InternalAlignment(g51,g52)
    c: InternalAlignment(g53,g52)
    c: InternalAlignment(g54,g52)
    c: Block(g52)
    c: Weight(g55) = 1
    c: Equal(g55,g56)
    c: Equal(g55,g57)
    c: InternalAlignment(g55,g58)
    c: InternalAlignment(g56,g58)
    c: InternalAlignment(g57,g58)
    c: InternalAlignment(g59,g58)
    c: InternalAlignment(g60,g58)
    c: Block(g58)
    c: Weight(g61) = 1
    c: Equal(g61,g62)
    c: Equal(g61,g63)
    c: InternalAlignment(g61,g64)
    c: InternalAlignment(g62,g64)
    c: InternalAlignment(g63,g64)
    c: InternalAlignment(g65,g64)
    c: InternalAlignment(g66,g64)
    c: Block(g64)
    c: Weight(g67) = 1
    c: Equal(g67,g68)
    c: Equal(g67,g69)
    c: InternalAlignment(g67,g70)
    c: InternalAlignment(g68,g70)
    c: InternalAlignment(g69,g70)
    c: InternalAlignment(g71,g70)
    c: InternalAlignment(g72,g70)
    c: Block(g70)
    c: Weight(g73) = 1
    c: Equal(g73,g74)
    c: Equal(g73,g75)
    c: InternalAlignment(g73,g76)
    c: InternalAlignment(g74,g76)
    c: InternalAlignment(g75,g76)
    c: InternalAlignment(g77,g76)
    c: InternalAlignment(g78,g76)
    c: Weight(g79) = 1
    c: Equal(g79,g80)
    c: Equal(g79,g81)
    c: InternalAlignment(g79,g82)
    c: InternalAlignment(g80,g82)
    c: InternalAlignment(g81,g82)
    c: InternalAlignment(g83,g82)
    c: InternalAlignment(g84,g82)
    c: Block(g76)
    c: Block(g82)
    c: Coincident(g85,g76)
    c: Coincident(g85,g82)
    c: Vertical(g85)
    c: Coincident(g86,g76)
    c: Coincident(g86,g58)
    c: Coincident(g87,g58)
    c: Coincident(g87,g82)
    c: Weight(g88) = 1
    c: Equal(g88,g89)
    c: Equal(g88,g90)
    c: InternalAlignment(g88,g91)
    c: InternalAlignment(g89,g91)
    c: InternalAlignment(g90,g91)
    c: InternalAlignment(g92,g91)
    c: InternalAlignment(g93,g91)
    c: Weight(g94) = 1
    c: Equal(g94,g95)
    c: Equal(g94,g96)
    c: InternalAlignment(g94,g97)
    c: InternalAlignment(g95,g97)
    c: InternalAlignment(g96,g97)
    c: InternalAlignment(g98,g97)
    c: InternalAlignment(g99,g97)
    c: Block(g91)
    c: Block(g97)
    c: Coincident(g100,g91)
    c: Coincident(g100,g97)
    c: Vertical(g100)
    c: Coincident(g101,g91)
    c: Coincident(g101,g52)
    c: Coincident(g102,g52)
    c: Coincident(g102,g97)
    c: Weight(g103) = 1
    c: Equal(g103,g104)
    c: Equal(g103,g105)
    c: InternalAlignment(g103,g106)
    c: InternalAlignment(g104,g106)
    c: InternalAlignment(g105,g106)
    c: InternalAlignment(g107,g106)
    c: InternalAlignment(g108,g106)
    c: Weight(g109) = 1
    c: Equal(g109,g110)
    c: Equal(g109,g111)
    c: InternalAlignment(g109,g112)
    c: InternalAlignment(g110,g112)
    c: InternalAlignment(g111,g112)
    c: InternalAlignment(g113,g112)
    c: InternalAlignment(g114,g112)
    c: Block(g106)
    c: Block(g112)
    c: Coincident(g115,g106)
    c: Coincident(g115,g112)
    c: Vertical(g115)
    c: Coincident(g116,g112)
    c: Coincident(g116,g70)
    c: Coincident(g117,g70)
    c: Coincident(g117,g106)
    c: Weight(g118) = 1
    c: Equal(g118,g119)
    c: Equal(g118,g120)
    c: InternalAlignment(g118,g121)
    c: InternalAlignment(g119,g121)
    c: InternalAlignment(g120,g121)
    c: InternalAlignment(g122,g121)
    c: InternalAlignment(g123,g121)
    c: Weight(g124) = 1
    c: Equal(g124,g125)
    c: Equal(g124,g126)
    c: InternalAlignment(g124,g127)
    c: InternalAlignment(g125,g127)
    c: InternalAlignment(g126,g127)
    c: InternalAlignment(g128,g127)
    c: InternalAlignment(g129,g127)
    c: Block(g121)
    c: Block(g127)
    c: Coincident(g130,g121)
    c: Coincident(g130,g127)
    c: Vertical(g130)
    c: Coincident(g131,g127)
    c: Coincident(g131,g64)
    c: Coincident(g132,g64)
    c: Coincident(g132,g121)
    c: Weight(g133) = 1
    c: Equal(g133,g134)
    c: Equal(g133,g135)
    c: InternalAlignment(g133,g136)
    c: InternalAlignment(g134,g136)
    c: InternalAlignment(g135,g136)
    c: InternalAlignment(g137,g136)
    c: InternalAlignment(g138,g136)
    c: Weight(g139) = 1
    c: Equal(g139,g140)
    c: Equal(g139,g141)
    c: InternalAlignment(g139,g142)
    c: InternalAlignment(g140,g142)
    c: InternalAlignment(g141,g142)
    c: InternalAlignment(g143,g142)
    c: InternalAlignment(g144,g142)
    c: Weight(g145) = 1
    c: Equal(g145,g146)
    c: Equal(g145,g147)
    c: InternalAlignment(g145,g148)
    c: InternalAlignment(g146,g148)
    c: InternalAlignment(g147,g148)
    c: InternalAlignment(g149,g148)
    c: InternalAlignment(g150,g148)
    c: Weight(g151) = 1
    c: Equal(g151,g152)
    c: Equal(g151,g153)
    c: InternalAlignment(g151,g154)
    c: InternalAlignment(g152,g154)
    c: InternalAlignment(g153,g154)
    c: InternalAlignment(g155,g154)
    c: InternalAlignment(g156,g154)
    c: Block(g154)
    c: Block(g148)
    c: Block(g142)
    c: Block(g136)
    c: Coincident(g157,g31)
    c: Coincident(g157,g154)
    c: Coincident(g158,g154)
    c: Coincident(g158,g148)
    c: Horizontal(g158)
    c: Coincident(g159,g148)
    c: Coincident(g159,g31)
    c: Vertical(g159)
    c: Coincident(g160,g25)
    c: Coincident(g160,g142)
    c: Vertical(g160)
    c: Coincident(g161,g142)
    c: Coincident(g161,g136)
    c: Horizontal(g161)
    c: Coincident(g162,g136)
    c: Coincident(g162,g25)
    c: Weight(g163) = 1
    c: Equal(g163,g164)
    c: Equal(g163,g165)
    c: InternalAlignment(g163,g166)
    c: InternalAlignment(g164,g166)
    c: InternalAlignment(g165,g166)
    c: InternalAlignment(g167,g166)
    c: InternalAlignment(g168,g166)
    c: Weight(g169) = 1
    c: Equal(g169,g170)
    c: Equal(g169,g171)
    c: InternalAlignment(g169,g172)
    c: InternalAlignment(g170,g172)
    c: InternalAlignment(g171,g172)
    c: InternalAlignment(g173,g172)
    c: InternalAlignment(g174,g172)
    c: Weight(g175) = 1
    c: Equal(g175,g176)
    c: Equal(g175,g177)
    c: InternalAlignment(g175,g178)
    c: InternalAlignment(g176,g178)
    c: InternalAlignment(g177,g178)
    c: InternalAlignment(g179,g178)
    c: InternalAlignment(g180,g178)
    c: Weight(g181) = 1
    c: Equal(g181,g182)
    c: Equal(g181,g183)
    c: InternalAlignment(g181,g184)
    c: InternalAlignment(g182,g184)
    c: InternalAlignment(g183,g184)
    c: InternalAlignment(g185,g184)
    c: InternalAlignment(g186,g184)
    c: Block(g184)
    c: Block(g178)
    c: Block(g172)
    c: Block(g166)
    c: Coincident(g187,g184)
    c: Coincident(g187,g178)
    c: Horizontal(g187)
    c: Coincident(g188,g178)
    c: Coincident(g188,g13)
    c: Vertical(g188)
    c: Coincident(g189,g19)
    c: Coincident(g189,g172)
    c: Vertical(g189)
    c: Coincident(g190,g172)
    c: Coincident(g190,g166)
    c: Horizontal(g190)
    c: Coincident(g191,g166)
    c: Coincident(g191,g19)
    c: Coincident(g192,g13)
    c: Weight(g193) = 1
    c: Equal(g193,g194)
    c: Equal(g193,g195)
    c: InternalAlignment(g193,g196)
    c: InternalAlignment(g194,g196)
    c: InternalAlignment(g195,g196)
    c: InternalAlignment(g197,g196)
    c: InternalAlignment(g198,g196)
    c: Weight(g199) = 1
    c: Equal(g199,g200)
    c: Equal(g199,g201)
    c: InternalAlignment(g199,g202)
    c: InternalAlignment(g200,g202)
    c: InternalAlignment(g201,g202)
    c: InternalAlignment(g203,g202)
    c: InternalAlignment(g204,g202)
    c: Block(g202)
    c: Block(g196)
    c: Coincident(g205,g202)
    c: Coincident(g205,g37)
    c: Coincident(g206,g37)
    c: Coincident(g206,g196)
    c: Coincident(g207,g196)
    c: Coincident(g207,g202)
    c: Vertical(g207)
    c: Weight(g208) = 1
    c: Equal(g208,g209)
    c: Equal(g208,g210)
    c: InternalAlignment(g208,g211)
    c: InternalAlignment(g209,g211)
    c: InternalAlignment(g210,g211)
    c: InternalAlignment(g212,g211)
    c: InternalAlignment(g213,g211)
    c: Weight(g214) = 1
    c: Equal(g214,g215)
    c: Equal(g214,g216)
    c: InternalAlignment(g214,g217)
    c: InternalAlignment(g215,g217)
    c: InternalAlignment(g216,g217)
    c: InternalAlignment(g218,g217)
    c: InternalAlignment(g219,g217)
    c: Block(g217)
    c: Block(g211)
    c: Coincident(g220,g211)
    c: Coincident(g220,g43)
    c: Coincident(g221,g43)
    c: Coincident(g221,g217)
    c: Coincident(g222,g217)
    c: Coincident(g222,g211)
    c: Vertical(g222)
    c: Horizontal(g223)
    c: Block(g223)
    c: Vertical(g224)
    c: Block(g224)
    c: Block(g225)
    c: Weight(g226) = 1
    c: Equal(g226,g227)
    c: Equal(g226,g228)
    c: InternalAlignment(g226,g229)
    c: InternalAlignment(g227,g229)
    c: InternalAlignment(g228,g229)
    c: InternalAlignment(g230,g229)
    c: InternalAlignment(g231,g229)
    c: Weight(g232) = 1
    c: Equal(g232,g233)
    c: Equal(g232,g234)
    c: InternalAlignment(g232,g235)
    c: InternalAlignment(g233,g235)
    c: InternalAlignment(g234,g235)
    c: InternalAlignment(g236,g235)
    c: InternalAlignment(g237,g235)
    c: Weight(g238) = 1
    c: Equal(g238,g239)
    c: Equal(g238,g240)
    c: InternalAlignment(g238,g241)
    c: InternalAlignment(g239,g241)
    c: InternalAlignment(g240,g241)
    c: InternalAlignment(g242,g241)
    c: InternalAlignment(g243,g241)
    c: Weight(g244) = 1
    c: Equal(g244,g245)
    c: Equal(g244,g246)
    c: InternalAlignment(g244,g247)
    c: InternalAlignment(g245,g247)
    c: InternalAlignment(g246,g247)
    c: InternalAlignment(g248,g247)
    c: InternalAlignment(g249,g247)
    c: Block(g229)
    c: Block(g235)
    c: Block(g241)
    c: Block(g247)
    c: Coincident(g250,g235)
    c: Coincident(g250,g229)
    c: Horizontal(g250)
    c: Block(g192)
    c: Weight(g251) = 1
    c: Equal(g251,g252)
    c: Equal(g251,g253)
    c: InternalAlignment(g251,g254)
    c: InternalAlignment(g252,g254)
    c: InternalAlignment(g253,g254)
    c: InternalAlignment(g255,g254)
    c: InternalAlignment(g256,g254)
    c: Weight(g257) = 1
    c: Equal(g257,g258)
    c: Equal(g257,g259)
    c: InternalAlignment(g257,g260)
    c: InternalAlignment(g258,g260)
    c: InternalAlignment(g259,g260)
    c: InternalAlignment(g261,g260)
    c: InternalAlignment(g262,g260)
    c: Block(g254)
    c: Block(g260)
    c: Coincident(g263,g254)
    c: Coincident(g263,g260)
    c: Weight(g264) = 1
    c: Equal(g264,g265)
    c: Equal(g264,g266)
    c: InternalAlignment(g264,g267)
    c: InternalAlignment(g265,g267)
    c: InternalAlignment(g266,g267)
    c: InternalAlignment(g268,g267)
    c: InternalAlignment(g269,g267)
    c: Weight(g270) = 1
    c: Equal(g270,g271)
    c: Equal(g270,g272)
    c: InternalAlignment(g270,g273)
    c: InternalAlignment(g271,g273)
    c: InternalAlignment(g272,g273)
    c: InternalAlignment(g274,g273)
    c: InternalAlignment(g275,g273)
    c: Weight(g276) = 1
    c: Equal(g276,g277)
    c: Equal(g276,g278)
    c: InternalAlignment(g276,g279)
    c: InternalAlignment(g277,g279)
    c: InternalAlignment(g278,g279)
    c: InternalAlignment(g280,g279)
    c: InternalAlignment(g281,g279)
    c: Block(g279)
    c: Block(g273)
    c: Block(g267)
    c: Coincident(g282,g273)
    c: Coincident(g282,g267)
    c: Coincident(g283,g267)
    c: Coincident(g283,g279)
    c: Vertical(g283)
    c: Coincident(g284,g279)
    c: Coincident(g284,g273)
    c: Horizontal(g284)
    c: Weight(g285) = 1
    c: Equal(g285,g286)
    c: InternalAlignment(g285,g287)
    c: InternalAlignment(g286,g287)
    c: InternalAlignment(g288,g287)
    c: InternalAlignment(g289,g287)
    c: Weight(g290) = 1
    c: InternalAlignment(g291,g293)
    c: InternalAlignment(g292,g293)
    c: InternalAlignment(g294,g293)
    c: InternalAlignment(g295,g293)
    c: Weight(g296) = 1
    c: Equal(g296,g297)
    c: Equal(g296,g298)
    c: InternalAlignment(g296,g299)
    c: InternalAlignment(g297,g299)
    c: InternalAlignment(g298,g299)
    c: InternalAlignment(g300,g299)
    c: InternalAlignment(g301,g299)
    c: Equal(g302,g303)
    c: Equal(g302,g304)
    c: InternalAlignment(g302,g305)
    c: InternalAlignment(g303,g305)
    c: InternalAlignment(g304,g305)
    c: InternalAlignment(g306,g305)
    c: InternalAlignment(g307,g305)
    c: Block(g293)
    c: Block(g299)
    c: Block(g305)
    c: Block(g287)
    c: Coincident(g308,g287)
    c: Coincident(g308,g293)
    c: Horizontal(g308)
    c: Coincident(g309,g293)
    c: Coincident(g309,g299)
    c: Vertical(g309)
    c: Coincident(g310,g299)
    c: Coincident(g310,g305)
    c: Horizontal(g310)
    c: Coincident(g311,g305)
    c: Coincident(g311,g287)
    c: Weight(g312) = 1
    c: Equal(g312,g313)
    c: Equal(g312,g314)
    c: InternalAlignment(g312,g315)
    c: InternalAlignment(g313,g315)
    c: InternalAlignment(g314,g315)
    c: InternalAlignment(g316,g315)
    c: InternalAlignment(g317,g315)
    c: Weight(g318) = 1
    c: Equal(g318,g319)
    c: Equal(g318,g320)
    c: InternalAlignment(g318,g321)
    c: InternalAlignment(g319,g321)
    c: InternalAlignment(g320,g321)
    c: InternalAlignment(g322,g321)
    c: InternalAlignment(g323,g321)
    c: Weight(g324) = 1
    c: Equal(g324,g325)
    c: Equal(g324,g326)
    c: InternalAlignment(g324,g327)
    c: InternalAlignment(g325,g327)
    c: InternalAlignment(g326,g327)
    c: InternalAlignment(g328,g327)
    c: InternalAlignment(g329,g327)
    c: Block(g327)
    c: Block(g321)
    c: Block(g315)
    c: Coincident(g330,g327)
    c: Coincident(g330,g321)
    c: Horizontal(g330)
    c: Coincident(g331,g321)
    c: Coincident(g331,g315)
    c: Vertical(g331)
    c: Coincident(g332,g315)
    c: Coincident(g332,g327)
    c: InternalAlignment(g333,g334)
    c: InternalAlignment(g335,g334)
    c: InternalAlignment(g336,g334)
    c: Block(g334)
    c: Equal(g337,g338)
    c: Equal(g337,g339)
    c: InternalAlignment(g337,g340)
    c: InternalAlignment(g338,g340)
    c: InternalAlignment(g339,g340)
    c: InternalAlignment(g341,g340)
    c: InternalAlignment(g342,g340)
    c: Block(g340)
    c: Coincident(g343,g334)
    c: Horizontal(g343)
    c: Block(g343)
    c: Coincident(g344,g334)
    c: Coincident(g344,g260)
    c: Vertical(g344)
    c: Coincident(g345,g340)
    c: Coincident(g345,g254)
    c: Vertical(g345)
    c: Coincident(g347,g5)
    c: Coincident(g348,g5)
    c: Block(g346)
    c: Block(g5)
    c: Block(g348)
    c: Block(g347)
    c: Distance(g344) = 119.89
FEATURE [Sketcher::SketchObject] Sketch001
  FullyConstrained = true
  MapMode = 4
  Placement = pos=(0,0,0) rot=(0.57735,0.57735,0.57735;2.0944rad)
  Support = -> [Sketch]
  sketch-geometry (46):
    g0: BSplineCurve PolesCount=3 KnotsCount=2 Degree=2 IsPeriodic=0
    g1: ArcOfCircle CenterX=73.1223 CenterY=-32.291 CenterZ=0 NormalX=0 NormalY=0 NormalZ=1 AngleXU=0 Radius=13 StartAngle=5.92268 EndAngle=9.06428
    g2: ArcOfCircle CenterX=66.7816 CenterY=-49.1439 CenterZ=0 NormalX=0 NormalY=0 NormalZ=1 AngleXU=0 Radius=13 StartAngle=2.78068 EndAngle=5.92131
    g3: ArcOfCircle CenterX=55.9263 CenterY=-78.1807 CenterZ=0 NormalX=0 NormalY=0 NormalZ=1 AngleXU=0 Radius=13 StartAngle=5.92268 EndAngle=9.06428
    g4: ArcOfCircle CenterX=49.5884 CenterY=-95.0342 CenterZ=0 NormalX=0 NormalY=0 NormalZ=1 AngleXU=0 Radius=13 StartAngle=2.78068 EndAngle=5.92131
    g5: ArcOfCircle CenterX=38.7206 CenterY=-124.067 CenterZ=0 NormalX=0 NormalY=0 NormalZ=1 AngleXU=0 Radius=13 StartAngle=5.92268 EndAngle=9.06428
    g6: ArcOfCircle CenterX=32.3875 CenterY=-140.92 CenterZ=0 NormalX=0 NormalY=0 NormalZ=1 AngleXU=0 Radius=13 StartAngle=2.78068 EndAngle=5.92131
    g7: ArcOfCircle CenterX=21.4715 CenterY=-169.934 CenterZ=0 NormalX=0 NormalY=0 NormalZ=1 AngleXU=0 Radius=13 StartAngle=5.92268 EndAngle=9.06428
    g8: ArcOfCircle CenterX=15.1336 CenterY=-186.787 CenterZ=0 NormalX=0 NormalY=0 NormalZ=1 AngleXU=0 Radius=13 StartAngle=2.78068 EndAngle=5.92131
    g9-g12: Circle x4 (B-spline internal-alignment scaffolding for g13; pole/knot coordinates omitted)
    g13: BSplineCurve PolesCount=4 KnotsCount=2 Degree=3 IsPeriodic=0
    g14: GeomPoint X=28.8094 Y=-19.0875 Z=0
    g15: GeomPoint X=47.0443 Y=-50.4712 Z=0
    g16: Circle CenterX=53.5586 CenterY=-23.2695 CenterZ=0 NormalX=0 NormalY=0 NormalZ=1 AngleXU=0 Radius=3.24518
    g17: Circle CenterX=-195.441 CenterY=-127.082 CenterZ=0 NormalX=0 NormalY=0 NormalZ=1 AngleXU=0 Radius=1
    g18: Circle CenterX=-8.24091 CenterY=-197.481 CenterZ=0 NormalX=0 NormalY=0 NormalZ=1 AngleXU=0 Radius=1
    g19: Circle CenterX=12.8789 CenterY=-141.321 CenterZ=0 NormalX=0 NormalY=0 NormalZ=1 AngleXU=0 Radius=1
    g20: BSplineCurve PolesCount=3 KnotsCount=2 Degree=2 IsPeriodic=0
    g21: GeomPoint X=-195.441 Y=-127.082 Z=0
    g22: GeomPoint X=12.8789 Y=-141.321 Z=0
    g23: Circle CenterX=-12.8016 CenterY=-179.036 CenterZ=0 NormalX=0 NormalY=0 NormalZ=1 AngleXU=0 Radius=10.5072
    g24: Circle CenterX=0.933922 CenterY=-166.43 CenterZ=0 NormalX=0 NormalY=0 NormalZ=1 AngleXU=0 Radius=3.26661
    g25: Circle CenterX=-33.5518 CenterY=-176.44 CenterZ=0 NormalX=0 NormalY=0 NormalZ=1 AngleXU=0 Radius=5.64388
    g26: Circle CenterX=-47.2366 CenterY=-173.859 CenterZ=0 NormalX=0 NormalY=0 NormalZ=1 AngleXU=0 Radius=3.01653
    g27: Circle CenterX=-56.2595 CenterY=-171.456 CenterZ=0 NormalX=0 NormalY=0 NormalZ=1 AngleXU=0 Radius=2.12826
    g28: ArcOfCircle CenterX=51.2151 CenterY=-198.473 CenterZ=0 NormalX=0 NormalY=0 NormalZ=1 AngleXU=0 Radius=20 StartAngle=2.78189 EndAngle=4.35269
    g29: LineSegment StartX=32.4951 StartY=-191.433 StartZ=0 EndX=94.6578 EndY=-26.1352 EndZ=0
    g30: LineSegment StartX=43.1192 StartY=-220.001 StartZ=0 EndX=-196.497 EndY=-129.89 EndZ=0
    g31: LineSegment StartX=43.1192 StartY=-220.001 StartZ=0 EndX=44.1752 EndY=-217.193 EndZ=0
    g32: LineSegment StartX=117.223 StartY=-19.0875 StartZ=0 EndX=117.223 EndY=-16.0875 EndZ=0
    g33: LineSegment StartX=117.223 StartY=-16.0875 StartZ=0 EndX=17.2232 EndY=-16.0875 EndZ=0
    g34: LineSegment StartX=17.2232 StartY=-16.0875 StartZ=0 EndX=17.2232 EndY=-19.0875 EndZ=0
    g35: LineSegment StartX=28.8094 StartY=-19.0875 StartZ=0 EndX=17.2232 EndY=-19.0875 EndZ=0
    g36: LineSegment StartX=47.0443 StartY=-50.4712 StartZ=0 EndX=12.8789 EndY=-141.321 EndZ=0
    g37: LineSegment StartX=-195.441 StartY=-127.082 StartZ=0 EndX=-196.497 EndY=-129.89 EndZ=0
    g38: LineSegment StartX=85.2866 StartY=-36.8766 StartZ=0 EndX=78.9396 EndY=-53.7463 EndZ=0
    g39: LineSegment StartX=60.9579 StartY=-27.7053 StartZ=0 EndX=54.6191 EndY=-44.5532 EndZ=0
    g40: LineSegment StartX=68.0907 StartY=-82.7664 StartZ=0 EndX=61.7465 EndY=-99.6365 EndZ=0
    g41: LineSegment StartX=43.7619 StartY=-73.595 StartZ=0 EndX=37.426 EndY=-90.4435 EndZ=0
    g42: LineSegment StartX=50.885 StartY=-128.652 StartZ=0 EndX=44.5456 EndY=-145.522 EndZ=0
    g43: LineSegment StartX=26.5562 StartY=-119.481 StartZ=0 EndX=20.2251 EndY=-136.329 EndZ=0
    g44: LineSegment StartX=9.3071 StartY=-165.349 StartZ=0 EndX=2.97115 EndY=-182.197 EndZ=0
    g45: LineSegment StartX=33.6358 StartY=-174.52 StartZ=0 EndX=27.2917 EndY=-191.39 EndZ=0
  constraints (71):
    c: Block(g0)
    c: Block(g1)
    c: Block(g2)
    c: Block(g4)
    c: Block(g3)
    c: Block(g6)
    c: Block(g5)
    c: Block(g8)
    c: Block(g7)
    c: Weight(g9) = 1
    c: Equal(g9,g10)
    c: Equal(g9,g11)
    c: Equal(g9,g12)
    c: InternalAlignment(g9-g12 -> g13) x4
    c: InternalAlignment(g14,g13)
    c: InternalAlignment(g15,g13)
    c: Block(g16)
    c: Weight(g17) = 1
    c: Equal(g17,g18)
    c: Equal(g17,g19)
    c: InternalAlignment(g17,g20)
    c: InternalAlignment(g18,g20)
    c: InternalAlignment(g19,g20)
    c: InternalAlignment(g21,g20)
    c: InternalAlignment(g22,g20)
    c: Block(g20)
    c: Block(g23)
    c: Block(g24)
    c: Block(g25)
    c: Block(g26)
    c: Block(g27)
    c: Block(g28)
    c: Coincident(g29,g28)
    c: Coincident(g29,g0)
    c: Block(g13)
    c: Coincident(g31,g30)
    c: Coincident(g31,g28)
    c: Block(g31)
    c: Coincident(g32,g0)
    c: Vertical(g32)
    c: Coincident(g33,g32)
    c: Horizontal(g33)
    c: Coincident(g34,g33)
    c: Vertical(g34)
    c: Block(g33)
    c: Coincident(g35,g13)
    c: Coincident(g35,g34)
    c: Horizontal(g35)
    c: Coincident(g36,g13)
    c: Coincident(g36,g20)
    c: Coincident(g37,g20)
    c: Coincident(g37,g30)
    c: Block(g30)
    c: Coincident(g38,g1)
    c: Coincident(g38,g2)
    c: Coincident(g39,g1)
    c: Coincident(g39,g2)
    c: Coincident(g40,g3)
    c: Coincident(g40,g4)
    c: Coincident(g41,g3)
    c: Coincident(g41,g4)
    c: Coincident(g42,g5)
    c: Coincident(g42,g6)
    c: Coincident(g43,g5)
    c: Coincident(g43,g6)
    c: Coincident(g44,g7)
    c: Coincident(g44,g8)
    c: Coincident(g45,g7)
    c: Coincident(g45,g8)
    c: Distance(g30) = 256
    c: Distance(g33) = 100
FEATURE [Part::Extrusion] Extrude002
  Base = -> Sketch001
  Dir = (1,0,0)
  DirMode = 2
  FaceMakerClass = Part::FaceMakerBullseye
  LengthFwd = 8
  LengthRev = 0
  Solid = true
  Symmetric = false
FEATURE [Sketcher::SketchObject] Sketch002
  FullyConstrained = true
  sketch-geometry (20):
    g0: LineSegment StartX=-2.77179 StartY=-200.304 StartZ=0 EndX=5.22821 EndY=-200.304 EndZ=0
    g1: LineSegment StartX=5.22821 StartY=-200.304 StartZ=0 EndX=5.22821 EndY=-197.304 EndZ=0
    g2: LineSegment StartX=-2.77179 StartY=-200.304 StartZ=0 EndX=-2.77179 EndY=-197.304 EndZ=0
    g3: LineSegment StartX=5.22821 StartY=-197.304 StartZ=0 EndX=8.22821 EndY=-197.304 EndZ=0
    g4: LineSegment StartX=-2.77179 StartY=-197.304 StartZ=0 EndX=-5.77179 EndY=-197.304 EndZ=0
    g5: LineSegment StartX=19.2282 StartY=-203.304 StartZ=0 EndX=19.2282 EndY=-206.304 EndZ=0
    g6: LineSegment StartX=-16.7718 StartY=-203.304 StartZ=0 EndX=-16.7718 EndY=-206.304 EndZ=0
    g7: LineSegment StartX=-16.7718 StartY=-206.304 StartZ=0 EndX=19.2282 EndY=-206.304 EndZ=0
    g8: Circle CenterX=-16.7718 CenterY=-203.304 CenterZ=0 NormalX=0 NormalY=0 NormalZ=1 AngleXU=0 Radius=1
    g9: Circle CenterX=-5.77179 CenterY=-203.304 CenterZ=0 NormalX=0 NormalY=0 NormalZ=1 AngleXU=0 Radius=1
    g10: Circle CenterX=-5.77179 CenterY=-197.304 CenterZ=0 NormalX=0 NormalY=0 NormalZ=1 AngleXU=0 Radius=1
    g11: BSplineCurve PolesCount=3 KnotsCount=2 Degree=2 IsPeriodic=0
    g12: GeomPoint X=-16.7718 Y=-203.304 Z=0
    g13: GeomPoint X=-5.77179 Y=-197.304 Z=0
    g14: Circle CenterX=19.2282 CenterY=-203.304 CenterZ=0 NormalX=0 NormalY=0 NormalZ=1 AngleXU=0 Radius=1
    g15: Circle CenterX=8.22821 CenterY=-203.304 CenterZ=0 NormalX=0 NormalY=0 NormalZ=1 AngleXU=0 Radius=1
    g16: Circle CenterX=8.22821 CenterY=-197.304 CenterZ=0 NormalX=0 NormalY=0 NormalZ=1 AngleXU=0 Radius=1
    g17: BSplineCurve PolesCount=3 KnotsCount=2 Degree=2 IsPeriodic=0
    g18: GeomPoint X=19.2282 Y=-203.304 Z=0
    g19: GeomPoint X=8.22821 Y=-197.304 Z=0
  constraints (41):
    c: Horizontal(g0)
    c: Distance(g0) = 8
    c: Coincident(g1,g0)
    c: Vertical(g1)
    c: Distance(g1) = 3
    c: Coincident(g2,g0)
    c: Vertical(g2)
    c: Distance(g2) = 3
    c: Coincident(g3,g1)
    c: Horizontal(g3)
    c: Distance(g3) = 3
    c: Coincident(g4,g2)
    c: Horizontal(g4)
    c: Distance(g4) = 3
    c: Vertical(g5)
    c: Vertical(g6)
    c: Coincident(g7,g6)
    c: Coincident(g7,g5)
    c: Weight(g8) = 1
    c: Equal(g8,g9)
    c: Equal(g8,g10)
    c: Coincident(g11,g4)
    c: InternalAlignment(g8,g11)
    c: InternalAlignment(g9,g11)
    c: InternalAlignment(g10,g11)
    c: InternalAlignment(g12,g11)
    c: InternalAlignment(g13,g11)
    c: Coincident(g17,g5)
    c: Weight(g14) = 1
    c: Equal(g14,g15)
    c: Equal(g14,g16)
    c: Coincident(g17,g3)
    c: InternalAlignment(g14,g17)
    c: InternalAlignment(g15,g17)
    c: InternalAlignment(g16,g17)
    c: InternalAlignment(g18,g17)
    c: InternalAlignment(g19,g17)
    c: Block(g7)
    c: Block(g17)
    c: Block(g11)
    c: Block(g6)
FEATURE [Part::Extrusion] Extrude003
  Base = -> Sketch002
  Dir = (0,0,1)
  DirMode = 2
  FaceMakerClass = Part::FaceMakerBullseye
  LengthFwd = 260
  LengthRev = 0
  Solid = true
  Symmetric = false
FEATURE [Sketcher::SketchObject] Sketch003
  FullyConstrained = false
  sketch-geometry (381):
    g0: LineSegment StartX=-42.9272 StartY=136.221 StartZ=0 EndX=-42.9272 EndY=-103.779 EndZ=0
    g1: LineSegment StartX=407.073 StartY=136.221 StartZ=0 EndX=407.073 EndY=-103.779 EndZ=0
    g2: ArcOfCircle CenterX=-26.9272 CenterY=-83.7794 CenterZ=0 NormalX=0 NormalY=0 NormalZ=1 AngleXU=0 Radius=8 StartAngle=3.14159 EndAngle=6.28319
    g3: ArcOfCircle CenterX=391.073 CenterY=-83.7794 CenterZ=0 NormalX=0 NormalY=0 NormalZ=1 AngleXU=0 Radius=8 StartAngle=3.14159 EndAngle=6.28319
    g4: Circle CenterX=175.022 CenterY=27.0628 CenterZ=0 NormalX=0 NormalY=0 NormalZ=1 AngleXU=0 Radius=1
    g5: Circle CenterX=179.022 CenterY=24.8665 CenterZ=0 NormalX=0 NormalY=0 NormalZ=1 AngleXU=0 Radius=1
    g6: Circle CenterX=179.022 CenterY=27.0628 CenterZ=0 NormalX=0 NormalY=0 NormalZ=1 AngleXU=0 Radius=1
    g7: BSplineCurve PolesCount=3 KnotsCount=2 Degree=2 IsPeriodic=0
    g8: GeomPoint X=175.022 Y=27.0628 Z=0
    g9: GeomPoint X=179.022 Y=27.0628 Z=0
    g10: Circle CenterX=189.124 CenterY=27.0628 CenterZ=0 NormalX=0 NormalY=0 NormalZ=1 AngleXU=0 Radius=1
    g11: Circle CenterX=185.124 CenterY=24.8665 CenterZ=0 NormalX=0 NormalY=0 NormalZ=1 AngleXU=0 Radius=1
    g12: Circle CenterX=185.124 CenterY=27.0628 CenterZ=0 NormalX=0 NormalY=0 NormalZ=1 AngleXU=0 Radius=1
    g13: BSplineCurve PolesCount=3 KnotsCount=2 Degree=2 IsPeriodic=0
    g14: GeomPoint X=189.124 Y=27.0628 Z=0
    g15: GeomPoint X=185.124 Y=27.0628 Z=0
    g16: Circle CenterX=175.022 CenterY=5.37834 CenterZ=0 NormalX=0 NormalY=0 NormalZ=1 AngleXU=0 Radius=1
    g17: Circle CenterX=179.022 CenterY=7.57463 CenterZ=0 NormalX=0 NormalY=0 NormalZ=1 AngleXU=0 Radius=1
    g18: Circle CenterX=179.022 CenterY=5.34704 CenterZ=0 NormalX=0 NormalY=0 NormalZ=1 AngleXU=0 Radius=1
    g19: BSplineCurve PolesCount=3 KnotsCount=2 Degree=2 IsPeriodic=0
    g20: GeomPoint X=175.022 Y=5.37834 Z=0
    g21: GeomPoint X=179.022 Y=5.34704 Z=0
    g22: Circle CenterX=189.124 CenterY=5.37834 CenterZ=0 NormalX=0 NormalY=0 NormalZ=1 AngleXU=0 Radius=1
    g23: Circle CenterX=185.124 CenterY=7.57463 CenterZ=0 NormalX=0 NormalY=0 NormalZ=1 AngleXU=0 Radius=1
    g24: Circle CenterX=185.124 CenterY=5.34704 CenterZ=0 NormalX=0 NormalY=0 NormalZ=1 AngleXU=0 Radius=1
    g25: BSplineCurve PolesCount=3 KnotsCount=2 Degree=2 IsPeriodic=0
    g26: GeomPoint X=189.124 Y=5.37834 Z=0
    g27: GeomPoint X=185.124 Y=5.34704 Z=0
    g28: Circle CenterX=165.871 CenterY=18.1458 CenterZ=0 NormalX=0 NormalY=0 NormalZ=1 AngleXU=0 Radius=1
    g29: Circle CenterX=169.377 CenterY=16.2206 CenterZ=0 NormalX=0 NormalY=0 NormalZ=1 AngleXU=0 Radius=1
    g30: Circle CenterX=165.871 CenterY=14.2954 CenterZ=0 NormalX=0 NormalY=0 NormalZ=1 AngleXU=0 Radius=1
    g31: BSplineCurve PolesCount=3 KnotsCount=2 Degree=2 IsPeriodic=0
    g32: GeomPoint X=165.871 Y=18.1458 Z=0
    g33: GeomPoint X=165.871 Y=14.2954 Z=0
    g34: Circle CenterX=198.275 CenterY=18.1458 CenterZ=0 NormalX=0 NormalY=0 NormalZ=1 AngleXU=0 Radius=1
    g35: Circle CenterX=194.768 CenterY=16.2206 CenterZ=0 NormalX=0 NormalY=0 NormalZ=1 AngleXU=0 Radius=1
    g36: Circle CenterX=198.275 CenterY=14.2954 CenterZ=0 NormalX=0 NormalY=0 NormalZ=1 AngleXU=0 Radius=1
    g37: BSplineCurve PolesCount=3 KnotsCount=2 Degree=2 IsPeriodic=0
    g38: GeomPoint X=198.275 Y=18.1458 Z=0
    g39: GeomPoint X=198.275 Y=14.2954 Z=0
    g40: LineSegment StartX=407.073 StartY=-103.779 StartZ=0 EndX=-42.9272 EndY=-103.779 EndZ=0
    g41: Circle CenterX=125.607 CenterY=54.1951 CenterZ=0 NormalX=0 NormalY=0 NormalZ=1 AngleXU=0 Radius=1
    g42: Circle CenterX=139.632 CenterY=46.4944 CenterZ=0 NormalX=0 NormalY=0 NormalZ=1 AngleXU=0 Radius=1
    g43: Circle CenterX=127.326 CenterY=56.7187 CenterZ=0 NormalX=0 NormalY=0 NormalZ=1 AngleXU=0 Radius=1
    g44: BSplineCurve PolesCount=3 KnotsCount=2 Degree=2 IsPeriodic=0
    g45: GeomPoint X=125.607 Y=54.1951 Z=0
    g46: GeomPoint X=127.326 Y=56.7187 Z=0
    g47: Circle CenterX=236.821 CenterY=56.7187 CenterZ=0 NormalX=0 NormalY=0 NormalZ=1 AngleXU=0 Radius=1
    g48: Circle CenterX=224.513 CenterY=46.4944 CenterZ=0 NormalX=0 NormalY=0 NormalZ=1 AngleXU=0 Radius=1
    g49: Circle CenterX=238.538 CenterY=54.1951 CenterZ=0 NormalX=0 NormalY=0 NormalZ=1 AngleXU=0 Radius=1
    g50: BSplineCurve PolesCount=3 KnotsCount=2 Degree=2 IsPeriodic=0
    g51: GeomPoint X=236.821 Y=56.7187 Z=0
    g52: GeomPoint X=238.538 Y=54.1951 Z=0
    g53: Circle CenterX=238.538 CenterY=-21.7539 CenterZ=0 NormalX=0 NormalY=0 NormalZ=1 AngleXU=0 Radius=1
    g54: Circle CenterX=224.513 CenterY=-14.0532 CenterZ=0 NormalX=0 NormalY=0 NormalZ=1 AngleXU=0 Radius=1
    g55: Circle CenterX=236.821 CenterY=-24.2775 CenterZ=0 NormalX=0 NormalY=0 NormalZ=1 AngleXU=0 Radius=1
    g56: BSplineCurve PolesCount=3 KnotsCount=2 Degree=2 IsPeriodic=0
    g57: GeomPoint X=238.538 Y=-21.7539 Z=0
    g58: GeomPoint X=236.821 Y=-24.2775 Z=0
    g59: Circle CenterX=125.607 CenterY=-21.7539 CenterZ=0 NormalX=0 NormalY=0 NormalZ=1 AngleXU=0 Radius=1
    g60: Circle CenterX=139.632 CenterY=-14.0532 CenterZ=0 NormalX=0 NormalY=0 NormalZ=1 AngleXU=0 Radius=1
    g61: Circle CenterX=127.325 CenterY=-24.2775 CenterZ=0 NormalX=0 NormalY=0 NormalZ=1 AngleXU=0 Radius=1
    g62: BSplineCurve PolesCount=3 KnotsCount=2 Degree=2 IsPeriodic=0
    g63: GeomPoint X=125.607 Y=-21.7539 Z=0
    g64: GeomPoint X=127.325 Y=-24.2775 Z=0
    g65: Circle CenterX=302.996 CenterY=111.695 CenterZ=0 NormalX=0 NormalY=0 NormalZ=1 AngleXU=0 Radius=1
    g66: Circle CenterX=306.073 CenterY=114.251 CenterZ=0 NormalX=0 NormalY=0 NormalZ=1 AngleXU=0 Radius=1
    g67: Circle CenterX=306.073 CenterY=110.251 CenterZ=0 NormalX=0 NormalY=0 NormalZ=1 AngleXU=0 Radius=1
    g68: BSplineCurve PolesCount=3 KnotsCount=2 Degree=2 IsPeriodic=0
    g69: GeomPoint X=302.996 Y=111.695 Z=0
    g70: GeomPoint X=306.073 Y=110.251 Z=0
    g71: Circle CenterX=306.073 CenterY=95.2763 CenterZ=0 NormalX=0 NormalY=0 NormalZ=1 AngleXU=0 Radius=1
    g72: Circle CenterX=306.073 CenterY=91.2763 CenterZ=0 NormalX=0 NormalY=0 NormalZ=1 AngleXU=0 Radius=1
    g73: Circle CenterX=302.567 CenterY=89.3511 CenterZ=0 NormalX=0 NormalY=0 NormalZ=1 AngleXU=0 Radius=1
    g74: BSplineCurve PolesCount=3 KnotsCount=2 Degree=2 IsPeriodic=0
    g75: GeomPoint X=306.073 Y=95.2763 Z=0
    g76: GeomPoint X=302.567 Y=89.3511 Z=0
    g77: LineSegment StartX=306.073 StartY=110.251 StartZ=0 EndX=306.073 EndY=95.2763 EndZ=0
    g78: LineSegment StartX=302.996 StartY=111.695 StartZ=0 EndX=236.821 EndY=56.7187 EndZ=0
    g79: LineSegment StartX=238.538 StartY=54.1951 StartZ=0 EndX=302.567 EndY=89.3511 EndZ=0
    g80: Circle CenterX=61.1496 CenterY=111.695 CenterZ=0 NormalX=0 NormalY=0 NormalZ=1 AngleXU=0 Radius=1
    g81: Circle CenterX=58.0728 CenterY=114.251 CenterZ=0 NormalX=0 NormalY=0 NormalZ=1 AngleXU=0 Radius=1
    g82: Circle CenterX=58.0728 CenterY=110.251 CenterZ=0 NormalX=0 NormalY=0 NormalZ=1 AngleXU=0 Radius=1
    g83: BSplineCurve PolesCount=3 KnotsCount=2 Degree=2 IsPeriodic=0
    g84: GeomPoint X=61.1496 Y=111.695 Z=0
    g85: GeomPoint X=58.0728 Y=110.251 Z=0
    g86: Circle CenterX=61.5791 CenterY=89.3511 CenterZ=0 NormalX=0 NormalY=0 NormalZ=1 AngleXU=0 Radius=1
    g87: Circle CenterX=58.0728 CenterY=91.2763 CenterZ=0 NormalX=0 NormalY=0 NormalZ=1 AngleXU=0 Radius=1
    g88: Circle CenterX=58.0728 CenterY=95.2763 CenterZ=0 NormalX=0 NormalY=0 NormalZ=1 AngleXU=0 Radius=1
    g89: BSplineCurve PolesCount=3 KnotsCount=2 Degree=2 IsPeriodic=0
    g90: GeomPoint X=61.5791 Y=89.3511 Z=0
    g91: GeomPoint X=58.0728 Y=95.2763 Z=0
    g92: LineSegment StartX=58.0728 StartY=110.251 StartZ=0 EndX=58.0728 EndY=95.2763 EndZ=0
    g93: LineSegment StartX=61.1496 StartY=111.695 StartZ=0 EndX=127.326 EndY=56.7187 EndZ=0
    g94: LineSegment StartX=125.607 StartY=54.1951 StartZ=0 EndX=61.5791 EndY=89.3511 EndZ=0
    g95: Circle CenterX=61.5791 CenterY=-56.9099 CenterZ=0 NormalX=0 NormalY=0 NormalZ=1 AngleXU=0 Radius=1
    g96: Circle CenterX=58.0728 CenterY=-58.8351 CenterZ=0 NormalX=0 NormalY=0 NormalZ=1 AngleXU=0 Radius=1
    g97: Circle CenterX=58.0728 CenterY=-62.8351 CenterZ=0 NormalX=0 NormalY=0 NormalZ=1 AngleXU=0 Radius=1
    g98: BSplineCurve PolesCount=3 KnotsCount=2 Degree=2 IsPeriodic=0
    g99: GeomPoint X=61.5791 Y=-56.9099 Z=0
    g100: GeomPoint X=58.0728 Y=-62.8351 Z=0
    g101: Circle CenterX=58.0728 CenterY=-77.8102 CenterZ=0 NormalX=0 NormalY=0 NormalZ=1 AngleXU=0 Radius=1
    g102: Circle CenterX=58.0728 CenterY=-81.8102 CenterZ=0 NormalX=0 NormalY=0 NormalZ=1 AngleXU=0 Radius=1
    g103: Circle CenterX=61.1496 CenterY=-79.2541 CenterZ=0 NormalX=0 NormalY=0 NormalZ=1 AngleXU=0 Radius=1
    g104: BSplineCurve PolesCount=3 KnotsCount=2 Degree=2 IsPeriodic=0
    g105: GeomPoint X=58.0728 Y=-77.8102 Z=0
    g106: GeomPoint X=61.1496 Y=-79.2541 Z=0
    g107: LineSegment StartX=58.0728 StartY=-62.8351 StartZ=0 EndX=58.0728 EndY=-77.8102 EndZ=0
    g108: LineSegment StartX=61.1496 StartY=-79.2541 StartZ=0 EndX=127.325 EndY=-24.2775 EndZ=0
    g109: LineSegment StartX=125.607 StartY=-21.7539 StartZ=0 EndX=61.5791 EndY=-56.9099 EndZ=0
    g110: Circle CenterX=302.567 CenterY=-56.9099 CenterZ=0 NormalX=0 NormalY=0 NormalZ=1 AngleXU=0 Radius=1
    g111: Circle CenterX=306.073 CenterY=-58.8351 CenterZ=0 NormalX=0 NormalY=0 NormalZ=1 AngleXU=0 Radius=1
    g112: Circle CenterX=306.073 CenterY=-62.8351 CenterZ=0 NormalX=0 NormalY=0 NormalZ=1 AngleXU=0 Radius=1
    g113: BSplineCurve PolesCount=3 KnotsCount=2 Degree=2 IsPeriodic=0
    g114: GeomPoint X=302.567 Y=-56.9099 Z=0
    g115: GeomPoint X=306.073 Y=-62.8351 Z=0
    g116: Circle CenterX=302.996 CenterY=-79.2541 CenterZ=0 NormalX=0 NormalY=0 NormalZ=1 AngleXU=0 Radius=1
    g117: Circle CenterX=306.073 CenterY=-81.8102 CenterZ=0 NormalX=0 NormalY=0 NormalZ=1 AngleXU=0 Radius=1
    g118: Circle CenterX=306.073 CenterY=-77.8102 CenterZ=0 NormalX=0 NormalY=0 NormalZ=1 AngleXU=0 Radius=1
    g119: BSplineCurve PolesCount=3 KnotsCount=2 Degree=2 IsPeriodic=0
    g120: GeomPoint X=302.996 Y=-79.2541 Z=0
    g121: GeomPoint X=306.073 Y=-77.8102 Z=0
    g122: LineSegment StartX=306.073 StartY=-62.8351 StartZ=0 EndX=306.073 EndY=-77.8102 EndZ=0
    g123: LineSegment StartX=302.996 StartY=-79.2541 StartZ=0 EndX=236.821 EndY=-24.2775 EndZ=0
    g124: LineSegment StartX=238.538 StartY=-21.7539 StartZ=0 EndX=302.567 EndY=-56.9099 EndZ=0
    g125: Circle CenterX=61.6457 CenterY=-88.8112 CenterZ=0 NormalX=0 NormalY=0 NormalZ=1 AngleXU=0 Radius=1
    g126: Circle CenterX=58.0728 CenterY=-91.7794 CenterZ=0 NormalX=0 NormalY=0 NormalZ=1 AngleXU=0 Radius=1
    g127: Circle CenterX=63.9135 CenterY=-91.7794 CenterZ=0 NormalX=0 NormalY=0 NormalZ=1 AngleXU=0 Radius=1
    g128: BSplineCurve PolesCount=3 KnotsCount=2 Degree=2 IsPeriodic=0
    g129: GeomPoint X=61.6457 Y=-88.8112 Z=0
    g130: GeomPoint X=63.9135 Y=-91.7794 Z=0
    g131: Circle CenterX=179.022 CenterY=-85.8163 CenterZ=0 NormalX=0 NormalY=0 NormalZ=1 AngleXU=0 Radius=1
    g132: Circle CenterX=179.022 CenterY=-91.7794 CenterZ=0 NormalX=0 NormalY=0 NormalZ=1 AngleXU=0 Radius=1
    g133: Circle CenterX=171.895 CenterY=-91.7794 CenterZ=0 NormalX=0 NormalY=0 NormalZ=1 AngleXU=0 Radius=1
    g134: BSplineCurve PolesCount=3 KnotsCount=2 Degree=2 IsPeriodic=0
    g135: GeomPoint X=179.022 Y=-85.8163 Z=0
    g136: GeomPoint X=171.895 Y=-91.7794 Z=0
    g137: Circle CenterX=185.124 CenterY=-86.2028 CenterZ=0 NormalX=0 NormalY=0 NormalZ=1 AngleXU=0 Radius=1
    g138: Circle CenterX=185.124 CenterY=-91.7794 CenterZ=0 NormalX=0 NormalY=0 NormalZ=1 AngleXU=0 Radius=1
    g139: Circle CenterX=191.747 CenterY=-91.7794 CenterZ=0 NormalX=0 NormalY=0 NormalZ=1 AngleXU=0 Radius=1
    g140: BSplineCurve PolesCount=3 KnotsCount=2 Degree=2 IsPeriodic=0
    g141: GeomPoint X=185.124 Y=-86.2028 Z=0
    g142: GeomPoint X=191.747 Y=-91.7794 Z=0
    g143: Circle CenterX=299.888 CenterY=-86.6413 CenterZ=0 NormalX=0 NormalY=0 NormalZ=1 AngleXU=0 Radius=1
    g144: Circle CenterX=306.073 CenterY=-91.7794 CenterZ=0 NormalX=0 NormalY=0 NormalZ=1 AngleXU=0 Radius=1
    g145: Circle CenterX=298.776 CenterY=-91.7794 CenterZ=0 NormalX=0 NormalY=0 NormalZ=1 AngleXU=0 Radius=1
    g146: BSplineCurve PolesCount=3 KnotsCount=2 Degree=2 IsPeriodic=0
    g147: GeomPoint X=299.888 Y=-86.6413 Z=0
    g148: GeomPoint X=298.776 Y=-91.7794 Z=0
    g149: LineSegment StartX=189.124 StartY=5.37834 StartZ=0 EndX=299.888 EndY=-86.6413 EndZ=0
    g150: LineSegment StartX=298.776 StartY=-91.7794 StartZ=0 EndX=191.747 EndY=-91.7794 EndZ=0
    g151: LineSegment StartX=185.124 StartY=-86.2028 StartZ=0 EndX=185.124 EndY=5.34704 EndZ=0
    g152: LineSegment StartX=179.022 StartY=5.34704 StartZ=0 EndX=179.022 EndY=-85.8163 EndZ=0
    g153: LineSegment StartX=171.895 StartY=-91.7794 StartZ=0 EndX=63.9135 EndY=-91.7794 EndZ=0
    g154: LineSegment StartX=61.6457 StartY=-88.8112 StartZ=0 EndX=175.022 EndY=5.37834 EndZ=0
    g155: Circle CenterX=302.073 CenterY=124.221 CenterZ=0 NormalX=0 NormalY=0 NormalZ=1 AngleXU=0 Radius=1
    g156: Circle CenterX=306.073 CenterY=124.221 CenterZ=0 NormalX=0 NormalY=0 NormalZ=1 AngleXU=0 Radius=1
    g157: Circle CenterX=302.996 CenterY=121.665 CenterZ=0 NormalX=0 NormalY=0 NormalZ=1 AngleXU=0 Radius=1
    g158: BSplineCurve PolesCount=3 KnotsCount=2 Degree=2 IsPeriodic=0
    g159: GeomPoint X=302.073 Y=124.221 Z=0
    g160: GeomPoint X=302.996 Y=121.665 Z=0
    g161: Circle CenterX=189.124 CenterY=124.221 CenterZ=0 NormalX=0 NormalY=0 NormalZ=1 AngleXU=0 Radius=1
    g162: Circle CenterX=185.124 CenterY=124.221 CenterZ=0 NormalX=0 NormalY=0 NormalZ=1 AngleXU=0 Radius=1
    g163: Circle CenterX=185.124 CenterY=120.221 CenterZ=0 NormalX=0 NormalY=0 NormalZ=1 AngleXU=0 Radius=1
    g164: BSplineCurve PolesCount=3 KnotsCount=2 Degree=2 IsPeriodic=0
    g165: GeomPoint X=189.124 Y=124.221 Z=0
    g166: GeomPoint X=185.124 Y=120.221 Z=0
    g167: Circle CenterX=175.022 CenterY=124.221 CenterZ=0 NormalX=0 NormalY=0 NormalZ=1 AngleXU=0 Radius=1
    g168: Circle CenterX=179.022 CenterY=124.221 CenterZ=0 NormalX=0 NormalY=0 NormalZ=1 AngleXU=0 Radius=1
    g169: Circle CenterX=179.022 CenterY=120.221 CenterZ=0 NormalX=0 NormalY=0 NormalZ=1 AngleXU=0 Radius=1
    g170: BSplineCurve PolesCount=3 KnotsCount=2 Degree=2 IsPeriodic=0
    g171: GeomPoint X=175.022 Y=124.221 Z=0
    g172: GeomPoint X=179.022 Y=120.221 Z=0
    g173: Circle CenterX=62.0728 CenterY=124.221 CenterZ=0 NormalX=0 NormalY=0 NormalZ=1 AngleXU=0 Radius=1
    g174: Circle CenterX=58.0728 CenterY=124.221 CenterZ=0 NormalX=0 NormalY=0 NormalZ=1 AngleXU=0 Radius=1
    g175: Circle CenterX=61.1496 CenterY=121.665 CenterZ=0 NormalX=0 NormalY=0 NormalZ=1 AngleXU=0 Radius=1
    g176: BSplineCurve PolesCount=3 KnotsCount=2 Degree=2 IsPeriodic=0
    g177: GeomPoint X=62.0728 Y=124.221 Z=0
    g178: GeomPoint X=61.1496 Y=121.665 Z=0
    g179: LineSegment StartX=62.0728 StartY=124.221 StartZ=0 EndX=175.022 EndY=124.221 EndZ=0
    g180: LineSegment StartX=179.022 StartY=120.221 StartZ=0 EndX=179.022 EndY=27.0628 EndZ=0
    g181: LineSegment StartX=185.124 StartY=27.0628 StartZ=0 EndX=185.124 EndY=120.221 EndZ=0
    g182: LineSegment StartX=189.124 StartY=124.221 StartZ=0 EndX=302.073 EndY=124.221 EndZ=0
    g183: LineSegment StartX=302.996 StartY=121.665 StartZ=0 EndX=189.124 EndY=27.0628 EndZ=0
    g184: LineSegment StartX=175.022 StartY=27.0628 StartZ=0 EndX=61.1496 EndY=121.665 EndZ=0
    g185: Circle CenterX=61.5791 CenterY=75.4095 CenterZ=0 NormalX=0 NormalY=0 NormalZ=1 AngleXU=0 Radius=1
    g186: Circle CenterX=58.0728 CenterY=77.3346 CenterZ=0 NormalX=0 NormalY=0 NormalZ=1 AngleXU=0 Radius=1
    g187: Circle CenterX=58.0728 CenterY=73.3346 CenterZ=0 NormalX=0 NormalY=0 NormalZ=1 AngleXU=0 Radius=1
    g188: BSplineCurve PolesCount=3 KnotsCount=2 Degree=2 IsPeriodic=0
    g189: GeomPoint X=61.5791 Y=75.4095 Z=0
    g190: GeomPoint X=58.0728 Y=73.3346 Z=0
    g191: Circle CenterX=58.0728 CenterY=-40.8935 CenterZ=0 NormalX=0 NormalY=0 NormalZ=1 AngleXU=0 Radius=1
    g192: Circle CenterX=58.0728 CenterY=-44.8935 CenterZ=0 NormalX=0 NormalY=0 NormalZ=1 AngleXU=0 Radius=1
    g193: Circle CenterX=61.5791 CenterY=-42.9683 CenterZ=0 NormalX=0 NormalY=0 NormalZ=1 AngleXU=0 Radius=1
    g194: BSplineCurve PolesCount=3 KnotsCount=2 Degree=2 IsPeriodic=0
    g195: GeomPoint X=58.0728 Y=-40.8935 Z=0
    g196: GeomPoint X=61.5791 Y=-42.9683 Z=0
    g197: LineSegment StartX=61.5791 StartY=-42.9683 StartZ=0 EndX=165.871 EndY=14.2954 EndZ=0
    g198: LineSegment StartX=165.871 StartY=18.1458 StartZ=0 EndX=61.5791 EndY=75.4095 EndZ=0
    g199: LineSegment StartX=58.0728 StartY=73.3346 StartZ=0 EndX=58.0728 EndY=-40.8935 EndZ=0
    g200: Circle CenterX=302.567 CenterY=-42.9683 CenterZ=0 NormalX=0 NormalY=0 NormalZ=1 AngleXU=0 Radius=1
    g201: Circle CenterX=306.073 CenterY=-44.8935 CenterZ=0 NormalX=0 NormalY=0 NormalZ=1 AngleXU=0 Radius=1
    g202: Circle CenterX=306.073 CenterY=-40.8935 CenterZ=0 NormalX=0 NormalY=0 NormalZ=1 AngleXU=0 Radius=1
    g203: BSplineCurve PolesCount=3 KnotsCount=2 Degree=2 IsPeriodic=0
    g204: GeomPoint X=302.567 Y=-42.9683 Z=0
    g205: GeomPoint X=306.073 Y=-40.8935 Z=0
    g206: Circle CenterX=306.073 CenterY=73.3346 CenterZ=0 NormalX=0 NormalY=0 NormalZ=1 AngleXU=0 Radius=1
    g207: Circle CenterX=306.073 CenterY=77.3346 CenterZ=0 NormalX=0 NormalY=0 NormalZ=1 AngleXU=0 Radius=1
    g208: Circle CenterX=302.567 CenterY=75.4095 CenterZ=0 NormalX=0 NormalY=0 NormalZ=1 AngleXU=0 Radius=1
    g209: BSplineCurve PolesCount=3 KnotsCount=2 Degree=2 IsPeriodic=0
    g210: GeomPoint X=306.073 Y=73.3346 Z=0
    g211: GeomPoint X=302.567 Y=75.4095 Z=0
    g212: LineSegment StartX=302.567 StartY=-42.9683 StartZ=0 EndX=198.275 EndY=14.2954 EndZ=0
    g213: LineSegment StartX=198.275 StartY=18.1458 StartZ=0 EndX=302.567 EndY=75.4095 EndZ=0
    g214: LineSegment StartX=306.073 StartY=73.3346 StartZ=0 EndX=306.073 EndY=-40.8935 EndZ=0
    g215: LineSegment StartX=322.073 StartY=105.865 StartZ=0 EndX=328.643 EndY=105.865 EndZ=0
    g216: LineSegment StartX=318.073 StartY=120.221 StartZ=0 EndX=318.073 EndY=109.865 EndZ=0
    g217: LineSegment StartX=336.157 StartY=107.779 StartZ=0 EndX=362.567 EndY=122.294 EndZ=0
    g218: Circle CenterX=362.073 CenterY=124.221 CenterZ=0 NormalX=0 NormalY=0 NormalZ=1 AngleXU=0 Radius=1
    g219: Circle CenterX=366.073 CenterY=124.221 CenterZ=0 NormalX=0 NormalY=0 NormalZ=1 AngleXU=0 Radius=1
    g220: Circle CenterX=362.567 CenterY=122.294 CenterZ=0 NormalX=0 NormalY=0 NormalZ=1 AngleXU=0 Radius=1
    g221: BSplineCurve PolesCount=3 KnotsCount=2 Degree=2 IsPeriodic=0
    g222: GeomPoint X=362.073 Y=124.221 Z=0
    g223: GeomPoint X=362.567 Y=122.294 Z=0
    g224: Circle CenterX=322.073 CenterY=124.221 CenterZ=0 NormalX=0 NormalY=0 NormalZ=1 AngleXU=0 Radius=1
    g225: Circle CenterX=318.073 CenterY=124.221 CenterZ=0 NormalX=0 NormalY=0 NormalZ=1 AngleXU=0 Radius=1
    g226: Circle CenterX=318.073 CenterY=120.221 CenterZ=0 NormalX=0 NormalY=0 NormalZ=1 AngleXU=0 Radius=1
    g227: BSplineCurve PolesCount=3 KnotsCount=2 Degree=2 IsPeriodic=0
    g228: GeomPoint X=322.073 Y=124.221 Z=0
    g229: GeomPoint X=318.073 Y=120.221 Z=0
    g230: Circle CenterX=322.073 CenterY=105.865 CenterZ=0 NormalX=0 NormalY=0 NormalZ=1 AngleXU=0 Radius=1
    g231: Circle CenterX=318.073 CenterY=105.865 CenterZ=0 NormalX=0 NormalY=0 NormalZ=1 AngleXU=0 Radius=1
    g232: Circle CenterX=318.073 CenterY=109.865 CenterZ=0 NormalX=0 NormalY=0 NormalZ=1 AngleXU=0 Radius=1
    g233: BSplineCurve PolesCount=3 KnotsCount=2 Degree=2 IsPeriodic=0
    g234: GeomPoint X=322.073 Y=105.865 Z=0
    g235: GeomPoint X=318.073 Y=109.865 Z=0
    g236: Circle CenterX=336.157 CenterY=107.779 CenterZ=0 NormalX=0 NormalY=0 NormalZ=1 AngleXU=0 Radius=1
    g237: Circle CenterX=332.651 CenterY=105.853 CenterZ=0 NormalX=0 NormalY=0 NormalZ=1 AngleXU=0 Radius=1
    g238: Circle CenterX=328.643 CenterY=105.865 CenterZ=0 NormalX=0 NormalY=0 NormalZ=1 AngleXU=0 Radius=1
    g239: BSplineCurve PolesCount=3 KnotsCount=2 Degree=2 IsPeriodic=0
    g240: GeomPoint X=336.157 Y=107.779 Z=0
    g241: GeomPoint X=328.643 Y=105.865 Z=0
    g242: LineSegment StartX=322.073 StartY=124.221 StartZ=0 EndX=362.073 EndY=124.221 EndZ=0
    g243: Circle CenterX=371.567 CenterY=-80.8644 CenterZ=0 NormalX=0 NormalY=0 NormalZ=1 AngleXU=0 Radius=1
    g244: Circle CenterX=375.073 CenterY=-82.7896 CenterZ=0 NormalX=0 NormalY=0 NormalZ=1 AngleXU=0 Radius=1
    g245: Circle CenterX=375.073 CenterY=-78.7896 CenterZ=0 NormalX=0 NormalY=0 NormalZ=1 AngleXU=0 Radius=1
    g246: BSplineCurve PolesCount=3 KnotsCount=2 Degree=2 IsPeriodic=0
    g247: GeomPoint X=371.567 Y=-80.8644 Z=0
    g248: GeomPoint X=375.073 Y=-78.7896 Z=0
    g249: Circle CenterX=321.579 CenterY=-53.4075 CenterZ=0 NormalX=0 NormalY=0 NormalZ=1 AngleXU=0 Radius=1
    g250: Circle CenterX=318.073 CenterY=-51.4823 CenterZ=0 NormalX=0 NormalY=0 NormalZ=1 AngleXU=0 Radius=1
    g251: Circle CenterX=318.073 CenterY=-47.4805 CenterZ=0 NormalX=0 NormalY=0 NormalZ=1 AngleXU=0 Radius=1
    g252: BSplineCurve PolesCount=3 KnotsCount=2 Degree=2 IsPeriodic=0
    g253: GeomPoint X=321.579 Y=-53.4075 Z=0
    g254: GeomPoint X=318.073 Y=-47.4805 Z=0
    g255: LineSegment StartX=371.567 StartY=-80.8644 StartZ=0 EndX=321.579 EndY=-53.4075 EndZ=0
    g256: Circle CenterX=321.579 CenterY=-67.3492 CenterZ=0 NormalX=0 NormalY=0 NormalZ=1 AngleXU=0 Radius=1
    g257: Circle CenterX=318.073 CenterY=-65.424 CenterZ=0 NormalX=0 NormalY=0 NormalZ=1 AngleXU=0 Radius=1
    g258: Circle CenterX=318.073 CenterY=-69.424 CenterZ=0 NormalX=0 NormalY=0 NormalZ=1 AngleXU=0 Radius=1
    g259: BSplineCurve PolesCount=3 KnotsCount=2 Degree=2 IsPeriodic=0
    g260: GeomPoint X=321.579 Y=-67.3492 Z=0
    g261: GeomPoint X=318.073 Y=-69.424 Z=0
    g262: Circle CenterX=362.567 CenterY=-89.8542 CenterZ=0 NormalX=0 NormalY=0 NormalZ=1 AngleXU=0 Radius=1
    g263: Circle CenterX=366.073 CenterY=-91.7794 CenterZ=0 NormalX=0 NormalY=0 NormalZ=1 AngleXU=0 Radius=1
    g264: Circle CenterX=362.073 CenterY=-91.7794 CenterZ=0 NormalX=0 NormalY=0 NormalZ=1 AngleXU=0 Radius=1
    g265: BSplineCurve PolesCount=3 KnotsCount=2 Degree=2 IsPeriodic=0
    g266: GeomPoint X=362.567 Y=-89.8542 Z=0
    g267: GeomPoint X=362.073 Y=-91.7794 Z=0
    g268: Circle CenterX=322.073 CenterY=-91.7794 CenterZ=0 NormalX=0 NormalY=0 NormalZ=1 AngleXU=0 Radius=1
    g269: Circle CenterX=318.073 CenterY=-91.7794 CenterZ=0 NormalX=0 NormalY=0 NormalZ=1 AngleXU=0 Radius=1
    g270: Circle CenterX=318.073 CenterY=-87.7794 CenterZ=0 NormalX=0 NormalY=0 NormalZ=1 AngleXU=0 Radius=1
    g271: BSplineCurve PolesCount=3 KnotsCount=2 Degree=2 IsPeriodic=0
    g272: GeomPoint X=322.073 Y=-91.7794 Z=0
    g273: GeomPoint X=318.073 Y=-87.7794 Z=0
    g274: LineSegment StartX=362.567 StartY=-89.8542 StartZ=0 EndX=321.579 EndY=-67.3492 EndZ=0
    g275: LineSegment StartX=318.073 StartY=-69.424 StartZ=0 EndX=318.073 EndY=-87.7794 EndZ=0
    g276: LineSegment StartX=322.073 StartY=-91.7794 StartZ=0 EndX=362.073 EndY=-91.7794 EndZ=0
    g277: Circle CenterX=2.07281 CenterY=124.221 CenterZ=0 NormalX=0 NormalY=0 NormalZ=1 AngleXU=0 Radius=1
    g278: Circle CenterX=1.57905 CenterY=122.295 CenterZ=0 NormalX=0 NormalY=0 NormalZ=1 AngleXU=0 Radius=1
    g279: BSplineCurve PolesCount=3 KnotsCount=2 Degree=2 IsPeriodic=0
    g280: GeomPoint X=2.07281 Y=124.221 Z=0
    g281: GeomPoint X=1.57905 Y=122.295 Z=0
    g282: Circle CenterX=42.0728 CenterY=124.221 CenterZ=0 NormalX=0 NormalY=0 NormalZ=1 AngleXU=0 Radius=1
    g283: Circle CenterX=46.0728 CenterY=124.221 CenterZ=0 NormalX=0 NormalY=0 NormalZ=1 AngleXU=0 Radius=1
    g284: Circle CenterX=46.0728 CenterY=120.221 CenterZ=0 NormalX=0 NormalY=0 NormalZ=1 AngleXU=0 Radius=1
    g285: BSplineCurve PolesCount=3 KnotsCount=2 Degree=2 IsPeriodic=0
    g286: GeomPoint X=42.0728 Y=124.221 Z=0
    g287: GeomPoint X=46.0728 Y=120.221 Z=0
    g288: Circle CenterX=46.0728 CenterY=109.865 CenterZ=0 NormalX=0 NormalY=0 NormalZ=1 AngleXU=0 Radius=1
    g289: Circle CenterX=46.0728 CenterY=105.865 CenterZ=0 NormalX=0 NormalY=0 NormalZ=1 AngleXU=0 Radius=1
    g290: Circle CenterX=42.0728 CenterY=105.865 CenterZ=0 NormalX=0 NormalY=0 NormalZ=1 AngleXU=0 Radius=1
    g291: BSplineCurve PolesCount=3 KnotsCount=2 Degree=2 IsPeriodic=0
    g292: GeomPoint X=46.0728 Y=109.865 Z=0
    g293: GeomPoint X=42.0728 Y=105.865 Z=0
    g294: Circle CenterX=35.5028 CenterY=105.865 CenterZ=0 NormalX=0 NormalY=0 NormalZ=1 AngleXU=0 Radius=1
    g295: Circle CenterX=31.5028 CenterY=105.865 CenterZ=0 NormalX=0 NormalY=0 NormalZ=1 AngleXU=0 Radius=1
    g296: Circle CenterX=27.9965 CenterY=107.79 CenterZ=0 NormalX=0 NormalY=0 NormalZ=1 AngleXU=0 Radius=1
    g297: BSplineCurve PolesCount=3 KnotsCount=2 Degree=2 IsPeriodic=0
    g298: GeomPoint X=35.5028 Y=105.865 Z=0
    g299: GeomPoint X=27.9965 Y=107.79 Z=0
    g300: LineSegment StartX=2.07281 StartY=124.221 StartZ=0 EndX=42.0728 EndY=124.221 EndZ=0
    g301: LineSegment StartX=46.0728 StartY=120.221 StartZ=0 EndX=46.0728 EndY=109.865 EndZ=0
    g302: LineSegment StartX=42.0728 StartY=105.865 StartZ=0 EndX=35.5028 EndY=105.865 EndZ=0
    g303: LineSegment StartX=27.9965 StartY=107.79 StartZ=0 EndX=1.57905 EndY=122.295 EndZ=0
    g304: Circle CenterX=42.5666 CenterY=-67.3492 CenterZ=0 NormalX=0 NormalY=0 NormalZ=1 AngleXU=0 Radius=1
    g305: Circle CenterX=46.0728 CenterY=-65.424 CenterZ=0 NormalX=0 NormalY=0 NormalZ=1 AngleXU=0 Radius=1
    g306: Circle CenterX=46.0728 CenterY=-69.424 CenterZ=0 NormalX=0 NormalY=0 NormalZ=1 AngleXU=0 Radius=1
    g307: BSplineCurve PolesCount=3 KnotsCount=2 Degree=2 IsPeriodic=0
    g308: GeomPoint X=42.5666 Y=-67.3492 Z=0
    g309: GeomPoint X=46.0728 Y=-69.424 Z=0
    g310: Circle CenterX=46.0728 CenterY=-87.7794 CenterZ=0 NormalX=0 NormalY=0 NormalZ=1 AngleXU=0 Radius=1
    g311: Circle CenterX=46.0728 CenterY=-91.7794 CenterZ=0 NormalX=0 NormalY=0 NormalZ=1 AngleXU=0 Radius=1
    g312: Circle CenterX=42.0728 CenterY=-91.7794 CenterZ=0 NormalX=0 NormalY=0 NormalZ=1 AngleXU=0 Radius=1
    g313: BSplineCurve PolesCount=3 KnotsCount=2 Degree=2 IsPeriodic=0
    g314: GeomPoint X=46.0728 Y=-87.7794 Z=0
    g315: GeomPoint X=42.0728 Y=-91.7794 Z=0
    g316: Circle CenterX=2.07281 CenterY=-91.7794 CenterZ=0 NormalX=0 NormalY=0 NormalZ=1 AngleXU=0 Radius=1
    g317: Circle CenterX=-1.92719 CenterY=-91.7794 CenterZ=0 NormalX=0 NormalY=0 NormalZ=1 AngleXU=0 Radius=1
    g318: Circle CenterX=1.57905 CenterY=-89.8542 CenterZ=0 NormalX=0 NormalY=0 NormalZ=1 AngleXU=0 Radius=1
    g319: BSplineCurve PolesCount=3 KnotsCount=2 Degree=2 IsPeriodic=0
    g320: GeomPoint X=2.07281 Y=-91.7794 Z=0
    g321: GeomPoint X=1.57905 Y=-89.8542 Z=0
    g322: LineSegment StartX=2.07281 StartY=-91.7794 StartZ=0 EndX=42.0728 EndY=-91.7794 EndZ=0
    g323: LineSegment StartX=46.0728 StartY=-87.7794 StartZ=0 EndX=46.0728 EndY=-69.424 EndZ=0
    g324: LineSegment StartX=42.5666 StartY=-67.3492 StartZ=0 EndX=1.57905 EndY=-89.8542 EndZ=0
    g325: Circle CenterX=322.073 CenterY=76.4095 CenterZ=0 NormalX=0 NormalY=0 NormalZ=1 AngleXU=0 Radius=4
    g326: BSplineCurve PolesCount=3 KnotsCount=2 Degree=2 IsPeriodic=0
    g327: GeomPoint X=318.073 Y=72.4095 Z=0
    g328: GeomPoint X=322.073 Y=76.4095 Z=0
    g329: Circle CenterX=375.073 CenterY=72.4095 CenterZ=0 NormalX=0 NormalY=0 NormalZ=1 AngleXU=0 Radius=1
    g330: Circle CenterX=375.073 CenterY=76.4095 CenterZ=0 NormalX=0 NormalY=0 NormalZ=1 AngleXU=0 Radius=1
    g331: Circle CenterX=371.073 CenterY=76.4095 CenterZ=0 NormalX=0 NormalY=0 NormalZ=1 AngleXU=0 Radius=1
    g332: BSplineCurve PolesCount=3 KnotsCount=2 Degree=2 IsPeriodic=0
    g333: GeomPoint X=375.073 Y=72.4095 Z=0
    g334: GeomPoint X=371.073 Y=76.4095 Z=0
    g335: LineSegment StartX=322.073 StartY=76.4095 StartZ=0 EndX=371.073 EndY=76.4095 EndZ=0
    g336: LineSegment StartX=318.073 StartY=72.4095 StartZ=0 EndX=318.073 EndY=-47.4805 EndZ=0
    g337: LineSegment StartX=375.073 StartY=72.4095 StartZ=0 EndX=375.073 EndY=-78.7896 EndZ=0
    g338: ArcOfCircle CenterX=-26.9272 CenterY=22.1087 CenterZ=0 NormalX=0 NormalY=0 NormalZ=1 AngleXU=0 Radius=4 StartAngle=5e-16 EndAngle=3.14159
    g339: LineSegment StartX=-22.9272 StartY=22.1087 StartZ=0 EndX=-18.9272 EndY=-83.7794 EndZ=0
    g340: LineSegment StartX=-34.9272 StartY=-83.7794 StartZ=0 EndX=-30.9272 EndY=22.1087 EndZ=0
    g341: ArcOfCircle CenterX=391.073 CenterY=22.1087 CenterZ=0 NormalX=0 NormalY=0 NormalZ=1 AngleXU=0 Radius=4 StartAngle=0 EndAngle=3.14159
    g342: LineSegment StartX=387.073 StartY=22.1087 StartZ=0 EndX=383.073 EndY=-83.7794 EndZ=0
    g343: LineSegment StartX=395.073 StartY=22.1087 StartZ=0 EndX=399.073 EndY=-83.7794 EndZ=0
    g344: Circle CenterX=-10.9272 CenterY=-78.7794 CenterZ=0 NormalX=0 NormalY=0 NormalZ=1 AngleXU=0 Radius=1
    g345: Circle CenterX=-10.9272 CenterY=-82.7794 CenterZ=0 NormalX=0 NormalY=0 NormalZ=1 AngleXU=0 Radius=1
    g346: Circle CenterX=-7.42095 CenterY=-80.8542 CenterZ=0 NormalX=0 NormalY=0 NormalZ=1 AngleXU=0 Radius=1
    g347: BSplineCurve PolesCount=3 KnotsCount=2 Degree=2 IsPeriodic=0
    g348: GeomPoint X=-10.9272 Y=-78.7794 Z=0
    g349: GeomPoint X=-7.42095 Y=-80.8542 Z=0
    g350: Circle CenterX=42.5666 CenterY=-53.4075 CenterZ=0 NormalX=0 NormalY=0 NormalZ=1 AngleXU=0 Radius=1
    g351: Circle CenterX=46.0728 CenterY=-51.4823 CenterZ=0 NormalX=0 NormalY=0 NormalZ=1 AngleXU=0 Radius=1
    g352: Circle CenterX=46.0728 CenterY=-47.4823 CenterZ=0 NormalX=0 NormalY=0 NormalZ=1 AngleXU=0 Radius=1
    g353: BSplineCurve PolesCount=3 KnotsCount=2 Degree=2 IsPeriodic=0
    g354: GeomPoint X=42.5666 Y=-53.4075 Z=0
    g355: GeomPoint X=46.0728 Y=-47.4823 Z=0
    g356: Circle CenterX=46.0728 CenterY=72.4095 CenterZ=0 NormalX=0 NormalY=0 NormalZ=1 AngleXU=0 Radius=1
    g357: Circle CenterX=46.0728 CenterY=76.4095 CenterZ=0 NormalX=0 NormalY=0 NormalZ=1 AngleXU=0 Radius=1
    g358: Circle CenterX=42.0728 CenterY=76.4095 CenterZ=0 NormalX=0 NormalY=0 NormalZ=1 AngleXU=0 Radius=1
    g359: BSplineCurve PolesCount=3 KnotsCount=2 Degree=2 IsPeriodic=0
    g360: GeomPoint X=46.0728 Y=72.4095 Z=0
    g361: GeomPoint X=42.0728 Y=76.4095 Z=0
    g362: Circle CenterX=-6.92718 CenterY=76.4095 CenterZ=0 NormalX=0 NormalY=0 NormalZ=1 AngleXU=0 Radius=1
    g363: Circle CenterX=-10.9272 CenterY=76.4095 CenterZ=0 NormalX=0 NormalY=0 NormalZ=1 AngleXU=0 Radius=1
    g364: Circle CenterX=-10.9272 CenterY=72.4095 CenterZ=0 NormalX=0 NormalY=0 NormalZ=1 AngleXU=0 Radius=1
    g365: BSplineCurve PolesCount=3 KnotsCount=2 Degree=2 IsPeriodic=0
    g366: GeomPoint X=-6.92718 Y=76.4095 Z=0
    g367: GeomPoint X=-10.9272 Y=72.4095 Z=0
    g368: LineSegment StartX=-10.9272 StartY=72.4095 StartZ=0 EndX=-10.9272 EndY=-78.7794 EndZ=0
    g369: LineSegment StartX=-7.42095 StartY=-80.8542 StartZ=0 EndX=42.5666 EndY=-53.4075 EndZ=0
    g370: LineSegment StartX=46.0728 StartY=-47.4823 StartZ=0 EndX=46.0728 EndY=72.4095 EndZ=0
    g371: LineSegment StartX=42.0728 StartY=76.4095 StartZ=0 EndX=-6.92719 EndY=76.4095 EndZ=0
    g372: LineSegment StartX=182.072 StartY=136.221 StartZ=0 EndX=182.072 EndY=137.404 EndZ=0
    g373: LineSegment StartX=182.072 StartY=136.221 StartZ=0 EndX=232.072 EndY=136.221 EndZ=0
    g374: LineSegment StartX=182.072 StartY=136.221 StartZ=0 EndX=132.072 EndY=136.221 EndZ=0
    g375: LineSegment StartX=232.072 StartY=136.221 StartZ=0 EndX=232.072 EndY=-117.815 EndZ=0
    g376: LineSegment StartX=132.072 StartY=136.221 StartZ=0 EndX=132.072 EndY=-121.309 EndZ=0
    g377: LineSegment StartX=132.072 StartY=136.221 StartZ=0 EndX=119.072 EndY=136.221 EndZ=0
    g378: LineSegment StartX=232.072 StartY=136.221 StartZ=0 EndX=245.072 EndY=136.221 EndZ=0
    g379: LineSegment StartX=245.072 StartY=136.221 StartZ=0 EndX=245.072 EndY=-116.499 EndZ=0
    g380: LineSegment StartX=119.072 StartY=136.221 StartZ=0 EndX=119.072 EndY=-116.228 EndZ=0
  constraints (632):
    c: Vertical(g0)
    c: Vertical(g1)
    c: Block(g1)
    c: Block(g0)
    c: Weight(g4) = 1
    c: Equal(g4,g5)
    c: Equal(g4,g6)
    c: InternalAlignment(g4,g7)
    c: InternalAlignment(g5,g7)
    c: InternalAlignment(g6,g7)
    c: InternalAlignment(g8,g7)
    c: InternalAlignment(g9,g7)
    c: Weight(g10) = 1
    c: Equal(g10,g11)
    c: Equal(g10,g12)
    c: InternalAlignment(g10,g13)
    c: InternalAlignment(g11,g13)
    c: InternalAlignment(g12,g13)
    c: InternalAlignment(g14,g13)
    c: InternalAlignment(g15,g13)
    c: Block(g13)
    c: Block(g7)
    c: Weight(g16) = 1
    c: Equal(g16,g17)
    c: Equal(g16,g18)
    c: InternalAlignment(g16,g19)
    c: InternalAlignment(g17,g19)
    c: InternalAlignment(g18,g19)
    c: InternalAlignment(g20,g19)
    c: InternalAlignment(g21,g19)
    c: Weight(g22) = 1
    c: Equal(g22,g23)
    c: Equal(g22,g24)
    c: InternalAlignment(g22,g25)
    c: InternalAlignment(g23,g25)
    c: InternalAlignment(g24,g25)
    c: InternalAlignment(g26,g25)
    c: InternalAlignment(g27,g25)
    c: Block(g25)
    c: Block(g19)
    c: Weight(g28) = 1
    c: Equal(g28,g29)
    c: Equal(g28,g30)
    c: InternalAlignment(g28,g31)
    c: InternalAlignment(g29,g31)
    c: InternalAlignment(g30,g31)
    c: InternalAlignment(g32,g31)
    c: InternalAlignment(g33,g31)
    c: Weight(g34) = 1
    c: Equal(g34,g35)
    c: Equal(g34,g36)
    c: InternalAlignment(g34,g37)
    c: InternalAlignment(g35,g37)
    c: InternalAlignment(g36,g37)
    c: InternalAlignment(g38,g37)
    c: InternalAlignment(g39,g37)
    c: Block(g31)
    c: Block(g37)
    c: Coincident(g40,g1)
    c: Coincident(g40,g0)
    c: Horizontal(g40)
    c: Distance(g40) = 450
    c: Weight(g41) = 1
    c: Equal(g41,g42)
    c: Equal(g41,g43)
    c: InternalAlignment(g41,g44)
    c: InternalAlignment(g42,g44)
    c: InternalAlignment(g43,g44)
    c: InternalAlignment(g45,g44)
    c: InternalAlignment(g46,g44)
    c: Block(g44)
    c: Weight(g47) = 1
    c: Equal(g47,g48)
    c: Equal(g47,g49)
    c: InternalAlignment(g47,g50)
    c: InternalAlignment(g48,g50)
    c: InternalAlignment(g49,g50)
    c: InternalAlignment(g51,g50)
    c: InternalAlignment(g52,g50)
    c: Block(g50)
    c: Weight(g53) = 1
    c: Equal(g53,g54)
    c: Equal(g53,g55)
    c: InternalAlignment(g53,g56)
    c: InternalAlignment(g54,g56)
    c: InternalAlignment(g55,g56)
    c: InternalAlignment(g57,g56)
    c: InternalAlignment(g58,g56)
    c: Block(g56)
    c: Weight(g59) = 1
    c: Equal(g59,g60)
    c: Equal(g59,g61)
    c: InternalAlignment(g59,g62)
    c: InternalAlignment(g60,g62)
    c: InternalAlignment(g61,g62)
    c: InternalAlignment(g63,g62)
    c: InternalAlignment(g64,g62)
    c: Block(g62)
    c: Weight(g65) = 1
    c: Equal(g65,g66)
    c: Equal(g65,g67)
    c: InternalAlignment(g65,g68)
    c: InternalAlignment(g66,g68)
    c: InternalAlignment(g67,g68)
    c: InternalAlignment(g69,g68)
    c: InternalAlignment(g70,g68)
    c: Weight(g71) = 1
    c: Equal(g71,g72)
    c: Equal(g71,g73)
    c: InternalAlignment(g71,g74)
    c: InternalAlignment(g72,g74)
    c: InternalAlignment(g73,g74)
    c: InternalAlignment(g75,g74)
    c: InternalAlignment(g76,g74)
    c: Block(g68)
    c: Block(g74)
    c: Coincident(g77,g68)
    c: Coincident(g77,g74)
    c: Vertical(g77)
    c: Coincident(g78,g68)
    c: Coincident(g78,g50)
    c: Coincident(g79,g50)
    c: Coincident(g79,g74)
    c: Weight(g80) = 1
    c: Equal(g80,g81)
    c: Equal(g80,g82)
    c: InternalAlignment(g80,g83)
    c: InternalAlignment(g81,g83)
    c: InternalAlignment(g82,g83)
    c: InternalAlignment(g84,g83)
    c: InternalAlignment(g85,g83)
    c: Weight(g86) = 1
    c: Equal(g86,g87)
    c: Equal(g86,g88)
    c: InternalAlignment(g86,g89)
    c: InternalAlignment(g87,g89)
    c: InternalAlignment(g88,g89)
    c: InternalAlignment(g90,g89)
    c: InternalAlignment(g91,g89)
    c: Block(g83)
    c: Block(g89)
    c: Coincident(g92,g83)
    c: Coincident(g92,g89)
    c: Vertical(g92)
    c: Coincident(g93,g83)
    c: Coincident(g93,g44)
    c: Coincident(g94,g44)
    c: Coincident(g94,g89)
    c: Weight(g95) = 1
    c: Equal(g95,g96)
    c: Equal(g95,g97)
    c: InternalAlignment(g95,g98)
    c: InternalAlignment(g96,g98)
    c: InternalAlignment(g97,g98)
    c: InternalAlignment(g99,g98)
    c: InternalAlignment(g100,g98)
    c: Weight(g101) = 1
    c: Equal(g101,g102)
    c: Equal(g101,g103)
    c: InternalAlignment(g101,g104)
    c: InternalAlignment(g102,g104)
    c: InternalAlignment(g103,g104)
    c: InternalAlignment(g105,g104)
    c: InternalAlignment(g106,g104)
    c: Block(g98)
    c: Block(g104)
    c: Coincident(g107,g98)
    c: Coincident(g107,g104)
    c: Vertical(g107)
    c: Coincident(g108,g104)
    c: Coincident(g108,g62)
    c: Coincident(g109,g62)
    c: Coincident(g109,g98)
    c: Weight(g110) = 1
    c: Equal(g110,g111)
    c: Equal(g110,g112)
    c: InternalAlignment(g110,g113)
    c: InternalAlignment(g111,g113)
    c: InternalAlignment(g112,g113)
    c: InternalAlignment(g114,g113)
    c: InternalAlignment(g115,g113)
    c: Weight(g116) = 1
    c: Equal(g116,g117)
    c: Equal(g116,g118)
    c: InternalAlignment(g116,g119)
    c: InternalAlignment(g117,g119)
    c: InternalAlignment(g118,g119)
    c: InternalAlignment(g120,g119)
    c: InternalAlignment(g121,g119)
    c: Block(g113)
    c: Block(g119)
    c: Coincident(g122,g113)
    c: Coincident(g122,g119)
    c: Vertical(g122)
    c: Coincident(g123,g119)
    c: Coincident(g123,g56)
    c: Coincident(g124,g56)
    c: Coincident(g124,g113)
    c: Weight(g125) = 1
    c: Equal(g125,g126)
    c: Equal(g125,g127)
    c: InternalAlignment(g125,g128)
    c: InternalAlignment(g126,g128)
    c: InternalAlignment(g127,g128)
    c: InternalAlignment(g129,g128)
    c: InternalAlignment(g130,g128)
    c: Weight(g131) = 1
    c: Equal(g131,g132)
    c: Equal(g131,g133)
    c: InternalAlignment(g131,g134)
    c: InternalAlignment(g132,g134)
    c: InternalAlignment(g133,g134)
    c: InternalAlignment(g135,g134)
    c: InternalAlignment(g136,g134)
    c: Weight(g137) = 1
    c: Equal(g137,g138)
    c: Equal(g137,g139)
    c: InternalAlignment(g137,g140)
    c: InternalAlignment(g138,g140)
    c: InternalAlignment(g139,g140)
    c: InternalAlignment(g141,g140)
    c: InternalAlignment(g142,g140)
    c: Weight(g143) = 1
    c: Equal(g143,g144)
    c: Equal(g143,g145)
    c: InternalAlignment(g143,g146)
    c: InternalAlignment(g144,g146)
    c: InternalAlignment(g145,g146)
    c: InternalAlignment(g147,g146)
    c: InternalAlignment(g148,g146)
    c: Block(g146)
    c: Block(g140)
    c: Block(g134)
    c: Block(g128)
    c: Coincident(g149,g25)
    c: Coincident(g149,g146)
    c: Coincident(g150,g146)
    c: Coincident(g150,g140)
    c: Horizontal(g150)
    c: Coincident(g151,g140)
    c: Coincident(g151,g25)
    c: Vertical(g151)
    c: Coincident(g152,g19)
    c: Coincident(g152,g134)
    c: Vertical(g152)
    c: Coincident(g153,g134)
    c: Coincident(g153,g128)
    c: Horizontal(g153)
    c: Coincident(g154,g128)
    c: Coincident(g154,g19)
    c: Weight(g155) = 1
    c: Equal(g155,g156)
    c: Equal(g155,g157)
    c: InternalAlignment(g155,g158)
    c: InternalAlignment(g156,g158)
    c: InternalAlignment(g157,g158)
    c: InternalAlignment(g159,g158)
    c: InternalAlignment(g160,g158)
    c: Weight(g161) = 1
    c: Equal(g161,g162)
    c: Equal(g161,g163)
    c: InternalAlignment(g161,g164)
    c: InternalAlignment(g162,g164)
    c: InternalAlignment(g163,g164)
    c: InternalAlignment(g165,g164)
    c: InternalAlignment(g166,g164)
    c: Weight(g167) = 1
    c: Equal(g167,g168)
    c: Equal(g167,g169)
    c: InternalAlignment(g167,g170)
    c: InternalAlignment(g168,g170)
    c: InternalAlignment(g169,g170)
    c: InternalAlignment(g171,g170)
    c: InternalAlignment(g172,g170)
    c: Weight(g173) = 1
    c: Equal(g173,g174)
    c: Equal(g173,g175)
    c: InternalAlignment(g173,g176)
    c: InternalAlignment(g174,g176)
    c: InternalAlignment(g175,g176)
    c: InternalAlignment(g177,g176)
    c: InternalAlignment(g178,g176)
    c: Block(g176)
    c: Block(g170)
    c: Block(g164)
    c: Block(g158)
    c: Coincident(g179,g176)
    c: Coincident(g179,g170)
    c: Horizontal(g179)
    c: Coincident(g180,g170)
    c: Coincident(g180,g7)
    c: Vertical(g180)
    c: Coincident(g181,g13)
    c: Coincident(g181,g164)
    c: Vertical(g181)
    c: Coincident(g182,g164)
    c: Coincident(g182,g158)
    c: Horizontal(g182)
    c: Coincident(g183,g158)
    c: Coincident(g183,g13)
    c: Coincident(g184,g7)
    c: Weight(g185) = 1
    c: Equal(g185,g186)
    c: Equal(g185,g187)
    c: InternalAlignment(g185,g188)
    c: InternalAlignment(g186,g188)
    c: InternalAlignment(g187,g188)
    c: InternalAlignment(g189,g188)
    c: InternalAlignment(g190,g188)
    c: Weight(g191) = 1
    c: Equal(g191,g192)
    c: Equal(g191,g193)
    c: InternalAlignment(g191,g194)
    c: InternalAlignment(g192,g194)
    c: InternalAlignment(g193,g194)
    c: InternalAlignment(g195,g194)
    c: InternalAlignment(g196,g194)
    c: Block(g194)
    c: Block(g188)
    c: Coincident(g197,g194)
    c: Coincident(g197,g31)
    c: Coincident(g198,g31)
    c: Coincident(g198,g188)
    c: Coincident(g199,g188)
    c: Coincident(g199,g194)
    c: Vertical(g199)
    c: Weight(g200) = 1
    c: Equal(g200,g201)
    c: Equal(g200,g202)
    c: InternalAlignment(g200,g203)
    c: InternalAlignment(g201,g203)
    c: InternalAlignment(g202,g203)
    c: InternalAlignment(g204,g203)
    c: InternalAlignment(g205,g203)
    c: Weight(g206) = 1
    c: Equal(g206,g207)
    c: Equal(g206,g208)
    c: InternalAlignment(g206,g209)
    c: InternalAlignment(g207,g209)
    c: InternalAlignment(g208,g209)
    c: InternalAlignment(g210,g209)
    c: InternalAlignment(g211,g209)
    c: Block(g209)
    c: Block(g203)
    c: Coincident(g212,g203)
    c: Coincident(g212,g37)
    c: Coincident(g213,g37)
    c: Coincident(g213,g209)
    c: Coincident(g214,g209)
    c: Coincident(g214,g203)
    c: Vertical(g214)
    c: Horizontal(g215)
    c: Block(g215)
    c: Vertical(g216)
    c: Block(g216)
    c: Block(g217)
    c: Weight(g218) = 1
    c: Equal(g218,g219)
    c: Equal(g218,g220)
    c: InternalAlignment(g218,g221)
    c: InternalAlignment(g219,g221)
    c: InternalAlignment(g220,g221)
    c: InternalAlignment(g222,g221)
    c: InternalAlignment(g223,g221)
    c: Weight(g224) = 1
    c: Equal(g224,g225)
    c: Equal(g224,g226)
    c: InternalAlignment(g224,g227)
    c: InternalAlignment(g225,g227)
    c: InternalAlignment(g226,g227)
    c: InternalAlignment(g228,g227)
    c: InternalAlignment(g229,g227)
    c: Weight(g230) = 1
    c: Equal(g230,g231)
    c: Equal(g230,g232)
    c: InternalAlignment(g230,g233)
    c: InternalAlignment(g231,g233)
    c: InternalAlignment(g232,g233)
    c: InternalAlignment(g234,g233)
    c: InternalAlignment(g235,g233)
    c: Weight(g236) = 1
    c: Equal(g236,g237)
    c: Equal(g236,g238)
    c: InternalAlignment(g236,g239)
    c: InternalAlignment(g237,g239)
    c: InternalAlignment(g238,g239)
    c: InternalAlignment(g240,g239)
    c: InternalAlignment(g241,g239)
    c: Block(g221)
    c: Block(g227)
    c: Block(g233)
    c: Block(g239)
    c: Coincident(g242,g227)
    c: Coincident(g242,g221)
    c: Horizontal(g242)
    c: Block(g184)
    c: Weight(g243) = 1
    c: Equal(g243,g244)
    c: Equal(g243,g245)
    c: InternalAlignment(g243,g246)
    c: InternalAlignment(g244,g246)
    c: InternalAlignment(g245,g246)
    c: InternalAlignment(g247,g246)
    c: InternalAlignment(g248,g246)
    c: Weight(g249) = 1
    c: Equal(g249,g250)
    c: Equal(g249,g251)
    c: InternalAlignment(g249,g252)
    c: InternalAlignment(g250,g252)
    c: InternalAlignment(g251,g252)
    c: InternalAlignment(g253,g252)
    c: InternalAlignment(g254,g252)
    c: Block(g246)
    c: Block(g252)
    c: Coincident(g255,g246)
    c: Coincident(g255,g252)
    c: Weight(g256) = 1
    c: Equal(g256,g257)
    c: Equal(g256,g258)
    c: InternalAlignment(g256,g259)
    c: InternalAlignment(g257,g259)
    c: InternalAlignment(g258,g259)
    c: InternalAlignment(g260,g259)
    c: InternalAlignment(g261,g259)
    c: Weight(g262) = 1
    c: Equal(g262,g263)
    c: Equal(g262,g264)
    c: InternalAlignment(g262,g265)
    c: InternalAlignment(g263,g265)
    c: InternalAlignment(g264,g265)
    c: InternalAlignment(g266,g265)
    c: InternalAlignment(g267,g265)
    c: Weight(g268) = 1
    c: Equal(g268,g269)
    c: Equal(g268,g270)
    c: InternalAlignment(g268,g271)
    c: InternalAlignment(g269,g271)
    c: InternalAlignment(g270,g271)
    c: InternalAlignment(g272,g271)
    c: InternalAlignment(g273,g271)
    c: Block(g271)
    c: Block(g265)
    c: Block(g259)
    c: Coincident(g274,g265)
    c: Coincident(g274,g259)
    c: Coincident(g275,g259)
    c: Coincident(g275,g271)
    c: Vertical(g275)
    c: Coincident(g276,g271)
    c: Coincident(g276,g265)
    c: Horizontal(g276)
    c: Weight(g277) = 1
    c: Equal(g277,g278)
    c: InternalAlignment(g277,g279)
    c: InternalAlignment(g278,g279)
    c: InternalAlignment(g280,g279)
    c: InternalAlignment(g281,g279)
    c: Weight(g282) = 1
    c: InternalAlignment(g283,g285)
    c: InternalAlignment(g284,g285)
    c: InternalAlignment(g286,g285)
    c: InternalAlignment(g287,g285)
    c: Weight(g288) = 1
    c: Equal(g288,g289)
    c: Equal(g288,g290)
    c: InternalAlignment(g288,g291)
    c: InternalAlignment(g289,g291)
    c: InternalAlignment(g290,g291)
    c: InternalAlignment(g292,g291)
    c: InternalAlignment(g293,g291)
    c: Equal(g294,g295)
    c: Equal(g294,g296)
    c: InternalAlignment(g294,g297)
    c: InternalAlignment(g295,g297)
    c: InternalAlignment(g296,g297)
    c: InternalAlignment(g298,g297)
    c: InternalAlignment(g299,g297)
    c: Block(g285)
    c: Block(g291)
    c: Block(g297)
    c: Block(g279)
    c: Coincident(g300,g279)
    c: Coincident(g300,g285)
    c: Horizontal(g300)
    c: Coincident(g301,g285)
    c: Coincident(g301,g291)
    c: Vertical(g301)
    c: Coincident(g302,g291)
    c: Coincident(g302,g297)
    c: Horizontal(g302)
    c: Coincident(g303,g297)
    c: Coincident(g303,g279)
    c: Weight(g304) = 1
    c: Equal(g304,g305)
    c: Equal(g304,g306)
    c: InternalAlignment(g304,g307)
    c: InternalAlignment(g305,g307)
    c: InternalAlignment(g306,g307)
    c: InternalAlignment(g308,g307)
    c: InternalAlignment(g309,g307)
    c: Weight(g310) = 1
    c: Equal(g310,g311)
    c: Equal(g310,g312)
    c: InternalAlignment(g310,g313)
    c: InternalAlignment(g311,g313)
    c: InternalAlignment(g312,g313)
    c: InternalAlignment(g314,g313)
    c: InternalAlignment(g315,g313)
    c: Weight(g316) = 1
    c: Equal(g316,g317)
    c: Equal(g316,g318)
    c: InternalAlignment(g316,g319)
    c: InternalAlignment(g317,g319)
    c: InternalAlignment(g318,g319)
    c: InternalAlignment(g320,g319)
    c: InternalAlignment(g321,g319)
    c: Block(g319)
    c: Block(g313)
    c: Block(g307)
    c: Coincident(g322,g319)
    c: Coincident(g322,g313)
    c: Horizontal(g322)
    c: Coincident(g323,g313)
    c: Coincident(g323,g307)
    c: Vertical(g323)
    c: Coincident(g324,g307)
    c: Coincident(g324,g319)
    c: InternalAlignment(g325,g326)
    c: InternalAlignment(g327,g326)
    c: InternalAlignment(g328,g326)
    c: Block(g326)
    c: Equal(g329,g330)
    c: Equal(g329,g331)
    c: InternalAlignment(g329,g332)
    c: InternalAlignment(g330,g332)
    c: InternalAlignment(g331,g332)
    c: InternalAlignment(g333,g332)
    c: InternalAlignment(g334,g332)
    c: Block(g332)
    c: Coincident(g335,g326)
    c: Horizontal(g335)
    c: Block(g335)
    c: Coincident(g336,g326)
    c: Coincident(g336,g252)
    c: Vertical(g336)
    c: Coincident(g337,g332)
    c: Coincident(g337,g246)
    c: Vertical(g337)
    c: Block(g338)
    c: Block(g2)
    c: Distance(g336) = 119.89
    c: Coincident(g339,g338)
    c: Coincident(g339,g2)
    c: Coincident(g340,g2)
    c: Coincident(g340,g338)
    c: Block(g3)
    c: Block(g341)
    c: Coincident(g342,g341)
    c: Coincident(g342,g3)
    c: Coincident(g343,g341)
    c: Coincident(g343,g3)
    c: Block(g343)
    c: Block(g342)
    c: Weight(g344) = 1
    c: Equal(g344,g345)
    c: Equal(g344,g346)
    c: InternalAlignment(g344,g347)
    c: InternalAlignment(g345,g347)
    c: InternalAlignment(g346,g347)
    c: InternalAlignment(g348,g347)
    c: InternalAlignment(g349,g347)
    c: Weight(g350) = 1
    c: Equal(g350,g351)
    c: Equal(g350,g352)
    c: InternalAlignment(g350,g353)
    c: InternalAlignment(g351,g353)
    c: InternalAlignment(g352,g353)
    c: InternalAlignment(g354,g353)
    c: InternalAlignment(g355,g353)
    c: Weight(g356) = 1
    c: Equal(g356,g357)
    c: Equal(g356,g358)
    c: InternalAlignment(g356,g359)
    c: InternalAlignment(g357,g359)
    c: InternalAlignment(g358,g359)
    c: InternalAlignment(g360,g359)
    c: InternalAlignment(g361,g359)
    c: Weight(g362) = 1
    c: Equal(g362,g363)
    c: Equal(g362,g364)
    c: InternalAlignment(g362,g365)
    c: InternalAlignment(g363,g365)
    c: InternalAlignment(g364,g365)
    c: InternalAlignment(g366,g365)
    c: InternalAlignment(g367,g365)
    c: Block(g365)
    c: Block(g359)
    c: Block(g353)
    c: Block(g347)
    c: Coincident(g368,g365)
    c: Coincident(g368,g347)
    c: Vertical(g368)
    c: Coincident(g369,g347)
    c: Coincident(g369,g353)
    c: Coincident(g370,g353)
    c: Coincident(g370,g359)
    c: Vertical(g370)
    c: Coincident(g371,g359)
    c: Coincident(g371,g365)
    c: Horizontal(g371)
    c: Vertical(g372)
    c: Block(g372)
    c: Coincident(g373,g372)
    c: Horizontal(g373)
    c: Distance(g373) = 50
    c: Coincident(g374,g372)
    c: Horizontal(g374)
    c: Distance(g374) = 50
    c: Coincident(g375,g373)
    c: Vertical(g375)
    c: Coincident(g376,g374)
    c: Vertical(g376)
    c: Coincident(g377,g374)
    c: Horizontal(g377)
    c: Distance(g377) = 13
    c: Coincident(g378,g373)
    c: Horizontal(g378)
    c: Distance(g378) = 13
    c: Coincident(g379,g378)
    c: Vertical(g379)
    c: Coincident(g380,g377)
    c: Vertical(g380)
FEATURE [Part::Extrusion] Extrude005
  Base = -> Sketch003
  Dir = (0,0,1)
  DirMode = 2
  FaceMakerClass = Part::FaceMakerBullseye
  LengthFwd = 24
  LengthRev = 0
  Solid = true
  Symmetric = false
